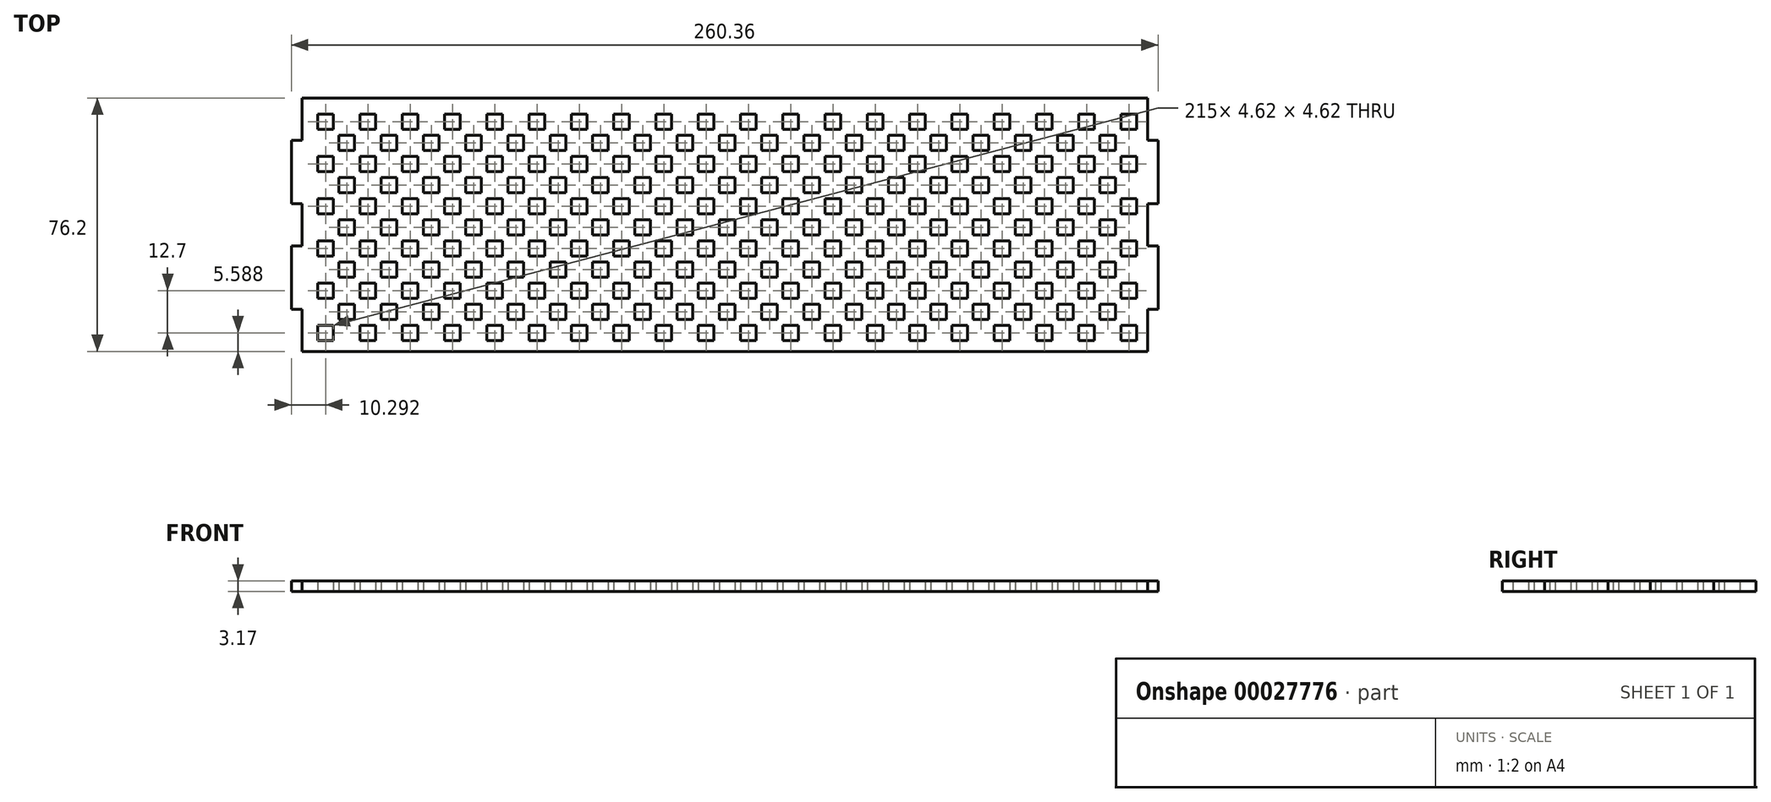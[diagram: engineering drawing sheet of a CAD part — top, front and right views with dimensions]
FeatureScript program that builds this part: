
annotation { "Feature Type Name" : "Feature", "Feature Type Description" : "" }
export const myFeature = defineFeature(function(context is Context, id is Id, definition is map)
    precondition{}
    {
        {
            var Q0;
            Q0=qCreatedBy(makeId("Top.planeOp"),FACE);
            var sketch = newSketch(context, id + "F0", { "sketchPlane" : qUnion([Q0])});
            skLineSegment(sketch, "E0.rect.bottom", {"start": v(-127, 38.1) * mm, "end": v(127, 38.1) * mm});
            skLineSegment(sketch, "E0.rect.top", {"start": v(-127, -38.1) * mm, "end": v(127, -38.1) * mm});
            skLineSegment(sketch, "E0.rect.left", {"start": v(-127, 38.1) * mm, "end": v(-127, 25.4) * mm});
            skLineSegment(sketch, "E0.rect.right", {"start": v(127, 38.1) * mm, "end": v(127, 25.4) * mm});
            skPoint(sketch, "E0.rect.middle", {"position": v(0, 0) * mm});
            skPoint(sketch, "E1", {"position": v(-127, 25.4) * mm});
            skPoint(sketch, "E2", {"position": v(-127, 6.35) * mm});
            skPoint(sketch, "E3", {"position": v(-127, -25.4) * mm});
            skPoint(sketch, "E4", {"position": v(-127, -6.35) * mm});
            skLineSegment(sketch, "E5.bottom", {"start": v(-127, 25.4) * mm, "end": v(-130.18, 25.4) * mm});
            skLineSegment(sketch, "E5.top", {"start": v(-127, 6.35) * mm, "end": v(-130.18, 6.35) * mm});
            skLineSegment(sketch, "E5.right", {"start": v(-130.18, 25.4) * mm, "end": v(-130.18, 6.35) * mm});
            skLineSegment(sketch, "E6.bottom", {"start": v(-127, -6.35) * mm, "end": v(-130.18, -6.35) * mm});
            skLineSegment(sketch, "E6.top", {"start": v(-127, -25.4) * mm, "end": v(-130.18, -25.4) * mm});
            skLineSegment(sketch, "E6.left", {"start": v(-127, -25.4) * mm, "end": v(-127, -25.4) * mm});
            skLineSegment(sketch, "E6.right", {"start": v(-130.18, -6.35) * mm, "end": v(-130.18, -25.4) * mm});
            skLineSegment(sketch, "E7.trimOffspring", {"start": v(-127, 6.35) * mm, "end": v(-127, -6.35) * mm});
            skLineSegment(sketch, "E8.trimOffspring", {"start": v(-127, -25.4) * mm, "end": v(-127, -38.1) * mm});
            skLineSegment(sketch, "E9.MirrorCS", {"start": v(130.18, 25.4) * mm, "end": v(130.18, 6.35) * mm});
            skLineSegment(sketch, "E10.MirrorCS", {"start": v(127, 25.4) * mm, "end": v(130.18, 25.4) * mm});
            skLineSegment(sketch, "E11.MirrorCS", {"start": v(127, 6.35) * mm, "end": v(130.18, 6.35) * mm});
            skLineSegment(sketch, "E12.MirrorCS", {"start": v(127, -6.35) * mm, "end": v(130.18, -6.35) * mm});
            skLineSegment(sketch, "E13.MirrorCS", {"start": v(130.18, -6.35) * mm, "end": v(130.18, -25.4) * mm});
            skLineSegment(sketch, "E14.MirrorCS", {"start": v(127, -25.4) * mm, "end": v(130.18, -25.4) * mm});
            skLineSegment(sketch, "E15.trimOffspring", {"start": v(127, 6.35) * mm, "end": v(127, -6.35) * mm});
            skLineSegment(sketch, "E16.trimOffspring", {"start": v(127, -25.4) * mm, "end": v(127, -38.1) * mm});
            skPoint(sketch, "E17", {"position": v(-127, 33.3) * mm});
            skPoint(sketch, "E18", {"position": v(-122.2, 38.1) * mm});
            skLineSegment(sketch, "E19.bottom", {"start": v(-122.2, 33.3) * mm, "end": v(-117.58, 33.3) * mm});
            skLineSegment(sketch, "E19.top", {"start": v(-122.2, 28.68) * mm, "end": v(-117.58, 28.68) * mm});
            skLineSegment(sketch, "E19.left", {"start": v(-122.2, 33.3) * mm, "end": v(-122.2, 28.68) * mm});
            skLineSegment(sketch, "E19.right", {"start": v(-117.58, 33.3) * mm, "end": v(-117.58, 28.68) * mm});
            skLineSegment(sketch, "E20.0.1.0", {"start": v(-117.58, 20.6) * mm, "end": v(-117.58, 15.98) * mm});
            skLineSegment(sketch, "E20.0.1.1", {"start": v(-122.2, 20.6) * mm, "end": v(-117.58, 20.6) * mm});
            skLineSegment(sketch, "E20.0.1.2", {"start": v(-122.2, 20.6) * mm, "end": v(-122.2, 15.98) * mm});
            skLineSegment(sketch, "E20.0.1.3", {"start": v(-122.2, 15.98) * mm, "end": v(-117.58, 15.98) * mm});
            skLineSegment(sketch, "E20.0.2.0", {"start": v(-117.58, 7.9) * mm, "end": v(-117.58, 3.28) * mm});
            skLineSegment(sketch, "E20.0.2.1", {"start": v(-122.2, 7.9) * mm, "end": v(-117.58, 7.9) * mm});
            skLineSegment(sketch, "E20.0.2.2", {"start": v(-122.2, 7.9) * mm, "end": v(-122.2, 3.28) * mm});
            skLineSegment(sketch, "E20.0.2.3", {"start": v(-122.2, 3.28) * mm, "end": v(-117.58, 3.28) * mm});
            skLineSegment(sketch, "E20.0.3.0", {"start": v(-117.58, -4.8) * mm, "end": v(-117.58, -9.42) * mm});
            skLineSegment(sketch, "E20.0.3.1", {"start": v(-122.2, -4.8) * mm, "end": v(-117.58, -4.8) * mm});
            skLineSegment(sketch, "E20.0.3.2", {"start": v(-122.2, -4.8) * mm, "end": v(-122.2, -9.42) * mm});
            skLineSegment(sketch, "E20.0.3.3", {"start": v(-122.2, -9.42) * mm, "end": v(-117.58, -9.42) * mm});
            skLineSegment(sketch, "E20.0.4.0", {"start": v(-117.58, -17.5) * mm, "end": v(-117.58, -22.12) * mm});
            skLineSegment(sketch, "E20.0.4.1", {"start": v(-122.2, -17.5) * mm, "end": v(-117.58, -17.5) * mm});
            skLineSegment(sketch, "E20.0.4.2", {"start": v(-122.2, -17.5) * mm, "end": v(-122.2, -22.12) * mm});
            skLineSegment(sketch, "E20.0.4.3", {"start": v(-122.2, -22.12) * mm, "end": v(-117.58, -22.12) * mm});
            skLineSegment(sketch, "E20.0.5.0", {"start": v(-117.58, -30.2) * mm, "end": v(-117.58, -34.82) * mm});
            skLineSegment(sketch, "E20.0.5.1", {"start": v(-122.2, -30.2) * mm, "end": v(-117.58, -30.2) * mm});
            skLineSegment(sketch, "E20.0.5.2", {"start": v(-122.2, -30.2) * mm, "end": v(-122.2, -34.82) * mm});
            skLineSegment(sketch, "E20.0.5.3", {"start": v(-122.2, -34.82) * mm, "end": v(-117.58, -34.82) * mm});
            skLineSegment(sketch, "E20.1.0.0", {"start": v(-104.88, 33.3) * mm, "end": v(-104.88, 28.68) * mm});
            skLineSegment(sketch, "E20.1.0.1", {"start": v(-109.5, 33.3) * mm, "end": v(-104.88, 33.3) * mm});
            skLineSegment(sketch, "E20.1.0.2", {"start": v(-109.5, 33.3) * mm, "end": v(-109.5, 28.68) * mm});
            skLineSegment(sketch, "E20.1.0.3", {"start": v(-109.5, 28.68) * mm, "end": v(-104.88, 28.68) * mm});
            skLineSegment(sketch, "E20.1.1.0", {"start": v(-104.88, 20.6) * mm, "end": v(-104.88, 15.98) * mm});
            skLineSegment(sketch, "E20.1.1.1", {"start": v(-109.5, 20.6) * mm, "end": v(-104.88, 20.6) * mm});
            skLineSegment(sketch, "E20.1.1.2", {"start": v(-109.5, 20.6) * mm, "end": v(-109.5, 15.98) * mm});
            skLineSegment(sketch, "E20.1.1.3", {"start": v(-109.5, 15.98) * mm, "end": v(-104.88, 15.98) * mm});
            skLineSegment(sketch, "E20.1.2.0", {"start": v(-104.88, 7.9) * mm, "end": v(-104.88, 3.28) * mm});
            skLineSegment(sketch, "E20.1.2.1", {"start": v(-109.5, 7.9) * mm, "end": v(-104.88, 7.9) * mm});
            skLineSegment(sketch, "E20.1.2.2", {"start": v(-109.5, 7.9) * mm, "end": v(-109.5, 3.28) * mm});
            skLineSegment(sketch, "E20.1.2.3", {"start": v(-109.5, 3.28) * mm, "end": v(-104.88, 3.28) * mm});
            skLineSegment(sketch, "E20.1.3.0", {"start": v(-104.88, -4.8) * mm, "end": v(-104.88, -9.42) * mm});
            skLineSegment(sketch, "E20.1.3.1", {"start": v(-109.5, -4.8) * mm, "end": v(-104.88, -4.8) * mm});
            skLineSegment(sketch, "E20.1.3.2", {"start": v(-109.5, -4.8) * mm, "end": v(-109.5, -9.42) * mm});
            skLineSegment(sketch, "E20.1.3.3", {"start": v(-109.5, -9.42) * mm, "end": v(-104.88, -9.42) * mm});
            skLineSegment(sketch, "E20.1.4.0", {"start": v(-104.88, -17.5) * mm, "end": v(-104.88, -22.12) * mm});
            skLineSegment(sketch, "E20.1.4.1", {"start": v(-109.5, -17.5) * mm, "end": v(-104.88, -17.5) * mm});
            skLineSegment(sketch, "E20.1.4.2", {"start": v(-109.5, -17.5) * mm, "end": v(-109.5, -22.12) * mm});
            skLineSegment(sketch, "E20.1.4.3", {"start": v(-109.5, -22.12) * mm, "end": v(-104.88, -22.12) * mm});
            skLineSegment(sketch, "E20.1.5.0", {"start": v(-104.88, -30.2) * mm, "end": v(-104.88, -34.82) * mm});
            skLineSegment(sketch, "E20.1.5.1", {"start": v(-109.5, -30.2) * mm, "end": v(-104.88, -30.2) * mm});
            skLineSegment(sketch, "E20.1.5.2", {"start": v(-109.5, -30.2) * mm, "end": v(-109.5, -34.82) * mm});
            skLineSegment(sketch, "E20.1.5.3", {"start": v(-109.5, -34.82) * mm, "end": v(-104.88, -34.82) * mm});
            skLineSegment(sketch, "E20.2.0.0", {"start": v(-92.18, 33.3) * mm, "end": v(-92.18, 28.68) * mm});
            skLineSegment(sketch, "E20.2.0.1", {"start": v(-96.8, 33.3) * mm, "end": v(-92.18, 33.3) * mm});
            skLineSegment(sketch, "E20.2.0.2", {"start": v(-96.8, 33.3) * mm, "end": v(-96.8, 28.68) * mm});
            skLineSegment(sketch, "E20.2.0.3", {"start": v(-96.8, 28.68) * mm, "end": v(-92.18, 28.68) * mm});
            skLineSegment(sketch, "E20.2.1.0", {"start": v(-92.18, 20.6) * mm, "end": v(-92.18, 15.98) * mm});
            skLineSegment(sketch, "E20.2.1.1", {"start": v(-96.8, 20.6) * mm, "end": v(-92.18, 20.6) * mm});
            skLineSegment(sketch, "E20.2.1.2", {"start": v(-96.8, 20.6) * mm, "end": v(-96.8, 15.98) * mm});
            skLineSegment(sketch, "E20.2.1.3", {"start": v(-96.8, 15.98) * mm, "end": v(-92.18, 15.98) * mm});
            skLineSegment(sketch, "E20.2.2.0", {"start": v(-92.18, 7.9) * mm, "end": v(-92.18, 3.28) * mm});
            skLineSegment(sketch, "E20.2.2.1", {"start": v(-96.8, 7.9) * mm, "end": v(-92.18, 7.9) * mm});
            skLineSegment(sketch, "E20.2.2.2", {"start": v(-96.8, 7.9) * mm, "end": v(-96.8, 3.28) * mm});
            skLineSegment(sketch, "E20.2.2.3", {"start": v(-96.8, 3.28) * mm, "end": v(-92.18, 3.28) * mm});
            skLineSegment(sketch, "E20.2.3.0", {"start": v(-92.18, -4.8) * mm, "end": v(-92.18, -9.42) * mm});
            skLineSegment(sketch, "E20.2.3.1", {"start": v(-96.8, -4.8) * mm, "end": v(-92.18, -4.8) * mm});
            skLineSegment(sketch, "E20.2.3.2", {"start": v(-96.8, -4.8) * mm, "end": v(-96.8, -9.42) * mm});
            skLineSegment(sketch, "E20.2.3.3", {"start": v(-96.8, -9.42) * mm, "end": v(-92.18, -9.42) * mm});
            skLineSegment(sketch, "E20.2.4.0", {"start": v(-92.18, -17.5) * mm, "end": v(-92.18, -22.12) * mm});
            skLineSegment(sketch, "E20.2.4.1", {"start": v(-96.8, -17.5) * mm, "end": v(-92.18, -17.5) * mm});
            skLineSegment(sketch, "E20.2.4.2", {"start": v(-96.8, -17.5) * mm, "end": v(-96.8, -22.12) * mm});
            skLineSegment(sketch, "E20.2.4.3", {"start": v(-96.8, -22.12) * mm, "end": v(-92.18, -22.12) * mm});
            skLineSegment(sketch, "E20.2.5.0", {"start": v(-92.18, -30.2) * mm, "end": v(-92.18, -34.82) * mm});
            skLineSegment(sketch, "E20.2.5.1", {"start": v(-96.8, -30.2) * mm, "end": v(-92.18, -30.2) * mm});
            skLineSegment(sketch, "E20.2.5.2", {"start": v(-96.8, -30.2) * mm, "end": v(-96.8, -34.82) * mm});
            skLineSegment(sketch, "E20.2.5.3", {"start": v(-96.8, -34.82) * mm, "end": v(-92.18, -34.82) * mm});
            skLineSegment(sketch, "E20.3.0.0", {"start": v(-79.48, 33.3) * mm, "end": v(-79.48, 28.68) * mm});
            skLineSegment(sketch, "E20.3.0.1", {"start": v(-84.1, 33.3) * mm, "end": v(-79.48, 33.3) * mm});
            skLineSegment(sketch, "E20.3.0.2", {"start": v(-84.1, 33.3) * mm, "end": v(-84.1, 28.68) * mm});
            skLineSegment(sketch, "E20.3.0.3", {"start": v(-84.1, 28.68) * mm, "end": v(-79.48, 28.68) * mm});
            skLineSegment(sketch, "E20.3.1.0", {"start": v(-79.48, 20.6) * mm, "end": v(-79.48, 15.98) * mm});
            skLineSegment(sketch, "E20.3.1.1", {"start": v(-84.1, 20.6) * mm, "end": v(-79.48, 20.6) * mm});
            skLineSegment(sketch, "E20.3.1.2", {"start": v(-84.1, 20.6) * mm, "end": v(-84.1, 15.98) * mm});
            skLineSegment(sketch, "E20.3.1.3", {"start": v(-84.1, 15.98) * mm, "end": v(-79.48, 15.98) * mm});
            skLineSegment(sketch, "E20.3.2.0", {"start": v(-79.48, 7.9) * mm, "end": v(-79.48, 3.28) * mm});
            skLineSegment(sketch, "E20.3.2.1", {"start": v(-84.1, 7.9) * mm, "end": v(-79.48, 7.9) * mm});
            skLineSegment(sketch, "E20.3.2.2", {"start": v(-84.1, 7.9) * mm, "end": v(-84.1, 3.28) * mm});
            skLineSegment(sketch, "E20.3.2.3", {"start": v(-84.1, 3.28) * mm, "end": v(-79.48, 3.28) * mm});
            skLineSegment(sketch, "E20.3.3.0", {"start": v(-79.48, -4.8) * mm, "end": v(-79.48, -9.42) * mm});
            skLineSegment(sketch, "E20.3.3.1", {"start": v(-84.1, -4.8) * mm, "end": v(-79.48, -4.8) * mm});
            skLineSegment(sketch, "E20.3.3.2", {"start": v(-84.1, -4.8) * mm, "end": v(-84.1, -9.42) * mm});
            skLineSegment(sketch, "E20.3.3.3", {"start": v(-84.1, -9.42) * mm, "end": v(-79.48, -9.42) * mm});
            skLineSegment(sketch, "E20.3.4.0", {"start": v(-79.48, -17.5) * mm, "end": v(-79.48, -22.12) * mm});
            skLineSegment(sketch, "E20.3.4.1", {"start": v(-84.1, -17.5) * mm, "end": v(-79.48, -17.5) * mm});
            skLineSegment(sketch, "E20.3.4.2", {"start": v(-84.1, -17.5) * mm, "end": v(-84.1, -22.12) * mm});
            skLineSegment(sketch, "E20.3.4.3", {"start": v(-84.1, -22.12) * mm, "end": v(-79.48, -22.12) * mm});
            skLineSegment(sketch, "E20.3.5.0", {"start": v(-79.48, -30.2) * mm, "end": v(-79.48, -34.82) * mm});
            skLineSegment(sketch, "E20.3.5.1", {"start": v(-84.1, -30.2) * mm, "end": v(-79.48, -30.2) * mm});
            skLineSegment(sketch, "E20.3.5.2", {"start": v(-84.1, -30.2) * mm, "end": v(-84.1, -34.82) * mm});
            skLineSegment(sketch, "E20.3.5.3", {"start": v(-84.1, -34.82) * mm, "end": v(-79.48, -34.82) * mm});
            skLineSegment(sketch, "E20.4.0.0", {"start": v(-66.78, 33.3) * mm, "end": v(-66.78, 28.68) * mm});
            skLineSegment(sketch, "E20.4.0.1", {"start": v(-71.4, 33.3) * mm, "end": v(-66.78, 33.3) * mm});
            skLineSegment(sketch, "E20.4.0.2", {"start": v(-71.4, 33.3) * mm, "end": v(-71.4, 28.68) * mm});
            skLineSegment(sketch, "E20.4.0.3", {"start": v(-71.4, 28.68) * mm, "end": v(-66.78, 28.68) * mm});
            skLineSegment(sketch, "E20.4.1.0", {"start": v(-66.78, 20.6) * mm, "end": v(-66.78, 15.98) * mm});
            skLineSegment(sketch, "E20.4.1.1", {"start": v(-71.4, 20.6) * mm, "end": v(-66.78, 20.6) * mm});
            skLineSegment(sketch, "E20.4.1.2", {"start": v(-71.4, 20.6) * mm, "end": v(-71.4, 15.98) * mm});
            skLineSegment(sketch, "E20.4.1.3", {"start": v(-71.4, 15.98) * mm, "end": v(-66.78, 15.98) * mm});
            skLineSegment(sketch, "E20.4.2.0", {"start": v(-66.78, 7.9) * mm, "end": v(-66.78, 3.28) * mm});
            skLineSegment(sketch, "E20.4.2.1", {"start": v(-71.4, 7.9) * mm, "end": v(-66.78, 7.9) * mm});
            skLineSegment(sketch, "E20.4.2.2", {"start": v(-71.4, 7.9) * mm, "end": v(-71.4, 3.28) * mm});
            skLineSegment(sketch, "E20.4.2.3", {"start": v(-71.4, 3.28) * mm, "end": v(-66.78, 3.28) * mm});
            skLineSegment(sketch, "E20.4.3.0", {"start": v(-66.78, -4.8) * mm, "end": v(-66.78, -9.42) * mm});
            skLineSegment(sketch, "E20.4.3.1", {"start": v(-71.4, -4.8) * mm, "end": v(-66.78, -4.8) * mm});
            skLineSegment(sketch, "E20.4.3.2", {"start": v(-71.4, -4.8) * mm, "end": v(-71.4, -9.42) * mm});
            skLineSegment(sketch, "E20.4.3.3", {"start": v(-71.4, -9.42) * mm, "end": v(-66.78, -9.42) * mm});
            skLineSegment(sketch, "E20.4.4.0", {"start": v(-66.78, -17.5) * mm, "end": v(-66.78, -22.12) * mm});
            skLineSegment(sketch, "E20.4.4.1", {"start": v(-71.4, -17.5) * mm, "end": v(-66.78, -17.5) * mm});
            skLineSegment(sketch, "E20.4.4.2", {"start": v(-71.4, -17.5) * mm, "end": v(-71.4, -22.12) * mm});
            skLineSegment(sketch, "E20.4.4.3", {"start": v(-71.4, -22.12) * mm, "end": v(-66.78, -22.12) * mm});
            skLineSegment(sketch, "E20.4.5.0", {"start": v(-66.78, -30.2) * mm, "end": v(-66.78, -34.82) * mm});
            skLineSegment(sketch, "E20.4.5.1", {"start": v(-71.4, -30.2) * mm, "end": v(-66.78, -30.2) * mm});
            skLineSegment(sketch, "E20.4.5.2", {"start": v(-71.4, -30.2) * mm, "end": v(-71.4, -34.82) * mm});
            skLineSegment(sketch, "E20.4.5.3", {"start": v(-71.4, -34.82) * mm, "end": v(-66.78, -34.82) * mm});
            skLineSegment(sketch, "E20.5.0.0", {"start": v(-54.08, 33.3) * mm, "end": v(-54.08, 28.68) * mm});
            skLineSegment(sketch, "E20.5.0.1", {"start": v(-58.7, 33.3) * mm, "end": v(-54.08, 33.3) * mm});
            skLineSegment(sketch, "E20.5.0.2", {"start": v(-58.7, 33.3) * mm, "end": v(-58.7, 28.68) * mm});
            skLineSegment(sketch, "E20.5.0.3", {"start": v(-58.7, 28.68) * mm, "end": v(-54.08, 28.68) * mm});
            skLineSegment(sketch, "E20.5.1.0", {"start": v(-54.08, 20.6) * mm, "end": v(-54.08, 15.98) * mm});
            skLineSegment(sketch, "E20.5.1.1", {"start": v(-58.7, 20.6) * mm, "end": v(-54.08, 20.6) * mm});
            skLineSegment(sketch, "E20.5.1.2", {"start": v(-58.7, 20.6) * mm, "end": v(-58.7, 15.98) * mm});
            skLineSegment(sketch, "E20.5.1.3", {"start": v(-58.7, 15.98) * mm, "end": v(-54.08, 15.98) * mm});
            skLineSegment(sketch, "E20.5.2.0", {"start": v(-54.08, 7.9) * mm, "end": v(-54.08, 3.28) * mm});
            skLineSegment(sketch, "E20.5.2.1", {"start": v(-58.7, 7.9) * mm, "end": v(-54.08, 7.9) * mm});
            skLineSegment(sketch, "E20.5.2.2", {"start": v(-58.7, 7.9) * mm, "end": v(-58.7, 3.28) * mm});
            skLineSegment(sketch, "E20.5.2.3", {"start": v(-58.7, 3.28) * mm, "end": v(-54.08, 3.28) * mm});
            skLineSegment(sketch, "E20.5.3.0", {"start": v(-54.08, -4.8) * mm, "end": v(-54.08, -9.42) * mm});
            skLineSegment(sketch, "E20.5.3.1", {"start": v(-58.7, -4.8) * mm, "end": v(-54.08, -4.8) * mm});
            skLineSegment(sketch, "E20.5.3.2", {"start": v(-58.7, -4.8) * mm, "end": v(-58.7, -9.42) * mm});
            skLineSegment(sketch, "E20.5.3.3", {"start": v(-58.7, -9.42) * mm, "end": v(-54.08, -9.42) * mm});
            skLineSegment(sketch, "E20.5.4.0", {"start": v(-54.08, -17.5) * mm, "end": v(-54.08, -22.12) * mm});
            skLineSegment(sketch, "E20.5.4.1", {"start": v(-58.7, -17.5) * mm, "end": v(-54.08, -17.5) * mm});
            skLineSegment(sketch, "E20.5.4.2", {"start": v(-58.7, -17.5) * mm, "end": v(-58.7, -22.12) * mm});
            skLineSegment(sketch, "E20.5.4.3", {"start": v(-58.7, -22.12) * mm, "end": v(-54.08, -22.12) * mm});
            skLineSegment(sketch, "E20.5.5.0", {"start": v(-54.08, -30.2) * mm, "end": v(-54.08, -34.82) * mm});
            skLineSegment(sketch, "E20.5.5.1", {"start": v(-58.7, -30.2) * mm, "end": v(-54.08, -30.2) * mm});
            skLineSegment(sketch, "E20.5.5.2", {"start": v(-58.7, -30.2) * mm, "end": v(-58.7, -34.82) * mm});
            skLineSegment(sketch, "E20.5.5.3", {"start": v(-58.7, -34.82) * mm, "end": v(-54.08, -34.82) * mm});
            skLineSegment(sketch, "E20.6.0.0", {"start": v(-41.38, 33.3) * mm, "end": v(-41.38, 28.68) * mm});
            skLineSegment(sketch, "E20.6.0.1", {"start": v(-46, 33.3) * mm, "end": v(-41.38, 33.3) * mm});
            skLineSegment(sketch, "E20.6.0.2", {"start": v(-46, 33.3) * mm, "end": v(-46, 28.68) * mm});
            skLineSegment(sketch, "E20.6.0.3", {"start": v(-46, 28.68) * mm, "end": v(-41.38, 28.68) * mm});
            skLineSegment(sketch, "E20.6.1.0", {"start": v(-41.38, 20.6) * mm, "end": v(-41.38, 15.98) * mm});
            skLineSegment(sketch, "E20.6.1.1", {"start": v(-46, 20.6) * mm, "end": v(-41.38, 20.6) * mm});
            skLineSegment(sketch, "E20.6.1.2", {"start": v(-46, 20.6) * mm, "end": v(-46, 15.98) * mm});
            skLineSegment(sketch, "E20.6.1.3", {"start": v(-46, 15.98) * mm, "end": v(-41.38, 15.98) * mm});
            skLineSegment(sketch, "E20.6.2.0", {"start": v(-41.38, 7.9) * mm, "end": v(-41.38, 3.28) * mm});
            skLineSegment(sketch, "E20.6.2.1", {"start": v(-46, 7.9) * mm, "end": v(-41.38, 7.9) * mm});
            skLineSegment(sketch, "E20.6.2.2", {"start": v(-46, 7.9) * mm, "end": v(-46, 3.28) * mm});
            skLineSegment(sketch, "E20.6.2.3", {"start": v(-46, 3.28) * mm, "end": v(-41.38, 3.28) * mm});
            skLineSegment(sketch, "E20.6.3.0", {"start": v(-41.38, -4.8) * mm, "end": v(-41.38, -9.42) * mm});
            skLineSegment(sketch, "E20.6.3.1", {"start": v(-46, -4.8) * mm, "end": v(-41.38, -4.8) * mm});
            skLineSegment(sketch, "E20.6.3.2", {"start": v(-46, -4.8) * mm, "end": v(-46, -9.42) * mm});
            skLineSegment(sketch, "E20.6.3.3", {"start": v(-46, -9.42) * mm, "end": v(-41.38, -9.42) * mm});
            skLineSegment(sketch, "E20.6.4.0", {"start": v(-41.38, -17.5) * mm, "end": v(-41.38, -22.12) * mm});
            skLineSegment(sketch, "E20.6.4.1", {"start": v(-46, -17.5) * mm, "end": v(-41.38, -17.5) * mm});
            skLineSegment(sketch, "E20.6.4.2", {"start": v(-46, -17.5) * mm, "end": v(-46, -22.12) * mm});
            skLineSegment(sketch, "E20.6.4.3", {"start": v(-46, -22.12) * mm, "end": v(-41.38, -22.12) * mm});
            skLineSegment(sketch, "E20.6.5.0", {"start": v(-41.38, -30.2) * mm, "end": v(-41.38, -34.82) * mm});
            skLineSegment(sketch, "E20.6.5.1", {"start": v(-46, -30.2) * mm, "end": v(-41.38, -30.2) * mm});
            skLineSegment(sketch, "E20.6.5.2", {"start": v(-46, -30.2) * mm, "end": v(-46, -34.82) * mm});
            skLineSegment(sketch, "E20.6.5.3", {"start": v(-46, -34.82) * mm, "end": v(-41.38, -34.82) * mm});
            skLineSegment(sketch, "E20.7.0.0", {"start": v(-28.68, 33.3) * mm, "end": v(-28.68, 28.68) * mm});
            skLineSegment(sketch, "E20.7.0.1", {"start": v(-33.3, 33.3) * mm, "end": v(-28.68, 33.3) * mm});
            skLineSegment(sketch, "E20.7.0.2", {"start": v(-33.3, 33.3) * mm, "end": v(-33.3, 28.68) * mm});
            skLineSegment(sketch, "E20.7.0.3", {"start": v(-33.3, 28.68) * mm, "end": v(-28.68, 28.68) * mm});
            skLineSegment(sketch, "E20.7.1.0", {"start": v(-28.68, 20.6) * mm, "end": v(-28.68, 15.98) * mm});
            skLineSegment(sketch, "E20.7.1.1", {"start": v(-33.3, 20.6) * mm, "end": v(-28.68, 20.6) * mm});
            skLineSegment(sketch, "E20.7.1.2", {"start": v(-33.3, 20.6) * mm, "end": v(-33.3, 15.98) * mm});
            skLineSegment(sketch, "E20.7.1.3", {"start": v(-33.3, 15.98) * mm, "end": v(-28.68, 15.98) * mm});
            skLineSegment(sketch, "E20.7.2.0", {"start": v(-28.68, 7.9) * mm, "end": v(-28.68, 3.28) * mm});
            skLineSegment(sketch, "E20.7.2.1", {"start": v(-33.3, 7.9) * mm, "end": v(-28.68, 7.9) * mm});
            skLineSegment(sketch, "E20.7.2.2", {"start": v(-33.3, 7.9) * mm, "end": v(-33.3, 3.28) * mm});
            skLineSegment(sketch, "E20.7.2.3", {"start": v(-33.3, 3.28) * mm, "end": v(-28.68, 3.28) * mm});
            skLineSegment(sketch, "E20.7.3.0", {"start": v(-28.68, -4.8) * mm, "end": v(-28.68, -9.42) * mm});
            skLineSegment(sketch, "E20.7.3.1", {"start": v(-33.3, -4.8) * mm, "end": v(-28.68, -4.8) * mm});
            skLineSegment(sketch, "E20.7.3.2", {"start": v(-33.3, -4.8) * mm, "end": v(-33.3, -9.42) * mm});
            skLineSegment(sketch, "E20.7.3.3", {"start": v(-33.3, -9.42) * mm, "end": v(-28.68, -9.42) * mm});
            skLineSegment(sketch, "E20.7.4.0", {"start": v(-28.68, -17.5) * mm, "end": v(-28.68, -22.12) * mm});
            skLineSegment(sketch, "E20.7.4.1", {"start": v(-33.3, -17.5) * mm, "end": v(-28.68, -17.5) * mm});
            skLineSegment(sketch, "E20.7.4.2", {"start": v(-33.3, -17.5) * mm, "end": v(-33.3, -22.12) * mm});
            skLineSegment(sketch, "E20.7.4.3", {"start": v(-33.3, -22.12) * mm, "end": v(-28.68, -22.12) * mm});
            skLineSegment(sketch, "E20.7.5.0", {"start": v(-28.68, -30.2) * mm, "end": v(-28.68, -34.82) * mm});
            skLineSegment(sketch, "E20.7.5.1", {"start": v(-33.3, -30.2) * mm, "end": v(-28.68, -30.2) * mm});
            skLineSegment(sketch, "E20.7.5.2", {"start": v(-33.3, -30.2) * mm, "end": v(-33.3, -34.82) * mm});
            skLineSegment(sketch, "E20.7.5.3", {"start": v(-33.3, -34.82) * mm, "end": v(-28.68, -34.82) * mm});
            skLineSegment(sketch, "E20.8.0.0", {"start": v(-15.98, 33.3) * mm, "end": v(-15.98, 28.68) * mm});
            skLineSegment(sketch, "E20.8.0.1", {"start": v(-20.6, 33.3) * mm, "end": v(-15.98, 33.3) * mm});
            skLineSegment(sketch, "E20.8.0.2", {"start": v(-20.6, 33.3) * mm, "end": v(-20.6, 28.68) * mm});
            skLineSegment(sketch, "E20.8.0.3", {"start": v(-20.6, 28.68) * mm, "end": v(-15.98, 28.68) * mm});
            skLineSegment(sketch, "E20.8.1.0", {"start": v(-15.98, 20.6) * mm, "end": v(-15.98, 15.98) * mm});
            skLineSegment(sketch, "E20.8.1.1", {"start": v(-20.6, 20.6) * mm, "end": v(-15.98, 20.6) * mm});
            skLineSegment(sketch, "E20.8.1.2", {"start": v(-20.6, 20.6) * mm, "end": v(-20.6, 15.98) * mm});
            skLineSegment(sketch, "E20.8.1.3", {"start": v(-20.6, 15.98) * mm, "end": v(-15.98, 15.98) * mm});
            skLineSegment(sketch, "E20.8.2.0", {"start": v(-15.98, 7.9) * mm, "end": v(-15.98, 3.28) * mm});
            skLineSegment(sketch, "E20.8.2.1", {"start": v(-20.6, 7.9) * mm, "end": v(-15.98, 7.9) * mm});
            skLineSegment(sketch, "E20.8.2.2", {"start": v(-20.6, 7.9) * mm, "end": v(-20.6, 3.28) * mm});
            skLineSegment(sketch, "E20.8.2.3", {"start": v(-20.6, 3.28) * mm, "end": v(-15.98, 3.28) * mm});
            skLineSegment(sketch, "E20.8.3.0", {"start": v(-15.98, -4.8) * mm, "end": v(-15.98, -9.42) * mm});
            skLineSegment(sketch, "E20.8.3.1", {"start": v(-20.6, -4.8) * mm, "end": v(-15.98, -4.8) * mm});
            skLineSegment(sketch, "E20.8.3.2", {"start": v(-20.6, -4.8) * mm, "end": v(-20.6, -9.42) * mm});
            skLineSegment(sketch, "E20.8.3.3", {"start": v(-20.6, -9.42) * mm, "end": v(-15.98, -9.42) * mm});
            skLineSegment(sketch, "E20.8.4.0", {"start": v(-15.98, -17.5) * mm, "end": v(-15.98, -22.12) * mm});
            skLineSegment(sketch, "E20.8.4.1", {"start": v(-20.6, -17.5) * mm, "end": v(-15.98, -17.5) * mm});
            skLineSegment(sketch, "E20.8.4.2", {"start": v(-20.6, -17.5) * mm, "end": v(-20.6, -22.12) * mm});
            skLineSegment(sketch, "E20.8.4.3", {"start": v(-20.6, -22.12) * mm, "end": v(-15.98, -22.12) * mm});
            skLineSegment(sketch, "E20.8.5.0", {"start": v(-15.98, -30.2) * mm, "end": v(-15.98, -34.82) * mm});
            skLineSegment(sketch, "E20.8.5.1", {"start": v(-20.6, -30.2) * mm, "end": v(-15.98, -30.2) * mm});
            skLineSegment(sketch, "E20.8.5.2", {"start": v(-20.6, -30.2) * mm, "end": v(-20.6, -34.82) * mm});
            skLineSegment(sketch, "E20.8.5.3", {"start": v(-20.6, -34.82) * mm, "end": v(-15.98, -34.82) * mm});
            skLineSegment(sketch, "E20.9.0.0", {"start": v(-3.28, 33.3) * mm, "end": v(-3.28, 28.68) * mm});
            skLineSegment(sketch, "E20.9.0.1", {"start": v(-7.9, 33.3) * mm, "end": v(-3.28, 33.3) * mm});
            skLineSegment(sketch, "E20.9.0.2", {"start": v(-7.9, 33.3) * mm, "end": v(-7.9, 28.68) * mm});
            skLineSegment(sketch, "E20.9.0.3", {"start": v(-7.9, 28.68) * mm, "end": v(-3.28, 28.68) * mm});
            skLineSegment(sketch, "E20.9.1.0", {"start": v(-3.28, 20.6) * mm, "end": v(-3.28, 15.98) * mm});
            skLineSegment(sketch, "E20.9.1.1", {"start": v(-7.9, 20.6) * mm, "end": v(-3.28, 20.6) * mm});
            skLineSegment(sketch, "E20.9.1.2", {"start": v(-7.9, 20.6) * mm, "end": v(-7.9, 15.98) * mm});
            skLineSegment(sketch, "E20.9.1.3", {"start": v(-7.9, 15.98) * mm, "end": v(-3.28, 15.98) * mm});
            skLineSegment(sketch, "E20.9.2.0", {"start": v(-3.28, 7.9) * mm, "end": v(-3.28, 3.28) * mm});
            skLineSegment(sketch, "E20.9.2.1", {"start": v(-7.9, 7.9) * mm, "end": v(-3.28, 7.9) * mm});
            skLineSegment(sketch, "E20.9.2.2", {"start": v(-7.9, 7.9) * mm, "end": v(-7.9, 3.28) * mm});
            skLineSegment(sketch, "E20.9.2.3", {"start": v(-7.9, 3.28) * mm, "end": v(-3.28, 3.28) * mm});
            skLineSegment(sketch, "E20.9.3.0", {"start": v(-3.28, -4.8) * mm, "end": v(-3.28, -9.42) * mm});
            skLineSegment(sketch, "E20.9.3.1", {"start": v(-7.9, -4.8) * mm, "end": v(-3.28, -4.8) * mm});
            skLineSegment(sketch, "E20.9.3.2", {"start": v(-7.9, -4.8) * mm, "end": v(-7.9, -9.42) * mm});
            skLineSegment(sketch, "E20.9.3.3", {"start": v(-7.9, -9.42) * mm, "end": v(-3.28, -9.42) * mm});
            skLineSegment(sketch, "E20.9.4.0", {"start": v(-3.28, -17.5) * mm, "end": v(-3.28, -22.12) * mm});
            skLineSegment(sketch, "E20.9.4.1", {"start": v(-7.9, -17.5) * mm, "end": v(-3.28, -17.5) * mm});
            skLineSegment(sketch, "E20.9.4.2", {"start": v(-7.9, -17.5) * mm, "end": v(-7.9, -22.12) * mm});
            skLineSegment(sketch, "E20.9.4.3", {"start": v(-7.9, -22.12) * mm, "end": v(-3.28, -22.12) * mm});
            skLineSegment(sketch, "E20.9.5.0", {"start": v(-3.28, -30.2) * mm, "end": v(-3.28, -34.82) * mm});
            skLineSegment(sketch, "E20.9.5.1", {"start": v(-7.9, -30.2) * mm, "end": v(-3.28, -30.2) * mm});
            skLineSegment(sketch, "E20.9.5.2", {"start": v(-7.9, -30.2) * mm, "end": v(-7.9, -34.82) * mm});
            skLineSegment(sketch, "E20.9.5.3", {"start": v(-7.9, -34.82) * mm, "end": v(-3.28, -34.82) * mm});
            skLineSegment(sketch, "E20.10.0.0", {"start": v(9.42, 33.3) * mm, "end": v(9.42, 28.68) * mm});
            skLineSegment(sketch, "E20.10.0.1", {"start": v(4.8, 33.3) * mm, "end": v(9.42, 33.3) * mm});
            skLineSegment(sketch, "E20.10.0.2", {"start": v(4.8, 33.3) * mm, "end": v(4.8, 28.68) * mm});
            skLineSegment(sketch, "E20.10.0.3", {"start": v(4.8, 28.68) * mm, "end": v(9.42, 28.68) * mm});
            skLineSegment(sketch, "E20.10.1.0", {"start": v(9.42, 20.6) * mm, "end": v(9.42, 15.98) * mm});
            skLineSegment(sketch, "E20.10.1.1", {"start": v(4.8, 20.6) * mm, "end": v(9.42, 20.6) * mm});
            skLineSegment(sketch, "E20.10.1.2", {"start": v(4.8, 20.6) * mm, "end": v(4.8, 15.98) * mm});
            skLineSegment(sketch, "E20.10.1.3", {"start": v(4.8, 15.98) * mm, "end": v(9.42, 15.98) * mm});
            skLineSegment(sketch, "E20.10.2.0", {"start": v(9.42, 7.9) * mm, "end": v(9.42, 3.28) * mm});
            skLineSegment(sketch, "E20.10.2.1", {"start": v(4.8, 7.9) * mm, "end": v(9.42, 7.9) * mm});
            skLineSegment(sketch, "E20.10.2.2", {"start": v(4.8, 7.9) * mm, "end": v(4.8, 3.28) * mm});
            skLineSegment(sketch, "E20.10.2.3", {"start": v(4.8, 3.28) * mm, "end": v(9.42, 3.28) * mm});
            skLineSegment(sketch, "E20.10.3.0", {"start": v(9.42, -4.8) * mm, "end": v(9.42, -9.42) * mm});
            skLineSegment(sketch, "E20.10.3.1", {"start": v(4.8, -4.8) * mm, "end": v(9.42, -4.8) * mm});
            skLineSegment(sketch, "E20.10.3.2", {"start": v(4.8, -4.8) * mm, "end": v(4.8, -9.42) * mm});
            skLineSegment(sketch, "E20.10.3.3", {"start": v(4.8, -9.42) * mm, "end": v(9.42, -9.42) * mm});
            skLineSegment(sketch, "E20.10.4.0", {"start": v(9.42, -17.5) * mm, "end": v(9.42, -22.12) * mm});
            skLineSegment(sketch, "E20.10.4.1", {"start": v(4.8, -17.5) * mm, "end": v(9.42, -17.5) * mm});
            skLineSegment(sketch, "E20.10.4.2", {"start": v(4.8, -17.5) * mm, "end": v(4.8, -22.12) * mm});
            skLineSegment(sketch, "E20.10.4.3", {"start": v(4.8, -22.12) * mm, "end": v(9.42, -22.12) * mm});
            skLineSegment(sketch, "E20.10.5.0", {"start": v(9.42, -30.2) * mm, "end": v(9.42, -34.82) * mm});
            skLineSegment(sketch, "E20.10.5.1", {"start": v(4.8, -30.2) * mm, "end": v(9.42, -30.2) * mm});
            skLineSegment(sketch, "E20.10.5.2", {"start": v(4.8, -30.2) * mm, "end": v(4.8, -34.82) * mm});
            skLineSegment(sketch, "E20.10.5.3", {"start": v(4.8, -34.82) * mm, "end": v(9.42, -34.82) * mm});
            skLineSegment(sketch, "E20.11.0.0", {"start": v(22.12, 33.3) * mm, "end": v(22.12, 28.68) * mm});
            skLineSegment(sketch, "E20.11.0.1", {"start": v(17.5, 33.3) * mm, "end": v(22.12, 33.3) * mm});
            skLineSegment(sketch, "E20.11.0.2", {"start": v(17.5, 33.3) * mm, "end": v(17.5, 28.68) * mm});
            skLineSegment(sketch, "E20.11.0.3", {"start": v(17.5, 28.68) * mm, "end": v(22.12, 28.68) * mm});
            skLineSegment(sketch, "E20.11.1.0", {"start": v(22.12, 20.6) * mm, "end": v(22.12, 15.98) * mm});
            skLineSegment(sketch, "E20.11.1.1", {"start": v(17.5, 20.6) * mm, "end": v(22.12, 20.6) * mm});
            skLineSegment(sketch, "E20.11.1.2", {"start": v(17.5, 20.6) * mm, "end": v(17.5, 15.98) * mm});
            skLineSegment(sketch, "E20.11.1.3", {"start": v(17.5, 15.98) * mm, "end": v(22.12, 15.98) * mm});
            skLineSegment(sketch, "E20.11.2.0", {"start": v(22.12, 7.9) * mm, "end": v(22.12, 3.28) * mm});
            skLineSegment(sketch, "E20.11.2.1", {"start": v(17.5, 7.9) * mm, "end": v(22.12, 7.9) * mm});
            skLineSegment(sketch, "E20.11.2.2", {"start": v(17.5, 7.9) * mm, "end": v(17.5, 3.28) * mm});
            skLineSegment(sketch, "E20.11.2.3", {"start": v(17.5, 3.28) * mm, "end": v(22.12, 3.28) * mm});
            skLineSegment(sketch, "E20.11.3.0", {"start": v(22.12, -4.8) * mm, "end": v(22.12, -9.42) * mm});
            skLineSegment(sketch, "E20.11.3.1", {"start": v(17.5, -4.8) * mm, "end": v(22.12, -4.8) * mm});
            skLineSegment(sketch, "E20.11.3.2", {"start": v(17.5, -4.8) * mm, "end": v(17.5, -9.42) * mm});
            skLineSegment(sketch, "E20.11.3.3", {"start": v(17.5, -9.42) * mm, "end": v(22.12, -9.42) * mm});
            skLineSegment(sketch, "E20.11.4.0", {"start": v(22.12, -17.5) * mm, "end": v(22.12, -22.12) * mm});
            skLineSegment(sketch, "E20.11.4.1", {"start": v(17.5, -17.5) * mm, "end": v(22.12, -17.5) * mm});
            skLineSegment(sketch, "E20.11.4.2", {"start": v(17.5, -17.5) * mm, "end": v(17.5, -22.12) * mm});
            skLineSegment(sketch, "E20.11.4.3", {"start": v(17.5, -22.12) * mm, "end": v(22.12, -22.12) * mm});
            skLineSegment(sketch, "E20.11.5.0", {"start": v(22.12, -30.2) * mm, "end": v(22.12, -34.82) * mm});
            skLineSegment(sketch, "E20.11.5.1", {"start": v(17.5, -30.2) * mm, "end": v(22.12, -30.2) * mm});
            skLineSegment(sketch, "E20.11.5.2", {"start": v(17.5, -30.2) * mm, "end": v(17.5, -34.82) * mm});
            skLineSegment(sketch, "E20.11.5.3", {"start": v(17.5, -34.82) * mm, "end": v(22.12, -34.82) * mm});
            skLineSegment(sketch, "E20.12.0.0", {"start": v(34.82, 33.3) * mm, "end": v(34.82, 28.68) * mm});
            skLineSegment(sketch, "E20.12.0.1", {"start": v(30.2, 33.3) * mm, "end": v(34.82, 33.3) * mm});
            skLineSegment(sketch, "E20.12.0.2", {"start": v(30.2, 33.3) * mm, "end": v(30.2, 28.68) * mm});
            skLineSegment(sketch, "E20.12.0.3", {"start": v(30.2, 28.68) * mm, "end": v(34.82, 28.68) * mm});
            skLineSegment(sketch, "E20.12.1.0", {"start": v(34.82, 20.6) * mm, "end": v(34.82, 15.98) * mm});
            skLineSegment(sketch, "E20.12.1.1", {"start": v(30.2, 20.6) * mm, "end": v(34.82, 20.6) * mm});
            skLineSegment(sketch, "E20.12.1.2", {"start": v(30.2, 20.6) * mm, "end": v(30.2, 15.98) * mm});
            skLineSegment(sketch, "E20.12.1.3", {"start": v(30.2, 15.98) * mm, "end": v(34.82, 15.98) * mm});
            skLineSegment(sketch, "E20.12.2.0", {"start": v(34.82, 7.9) * mm, "end": v(34.82, 3.28) * mm});
            skLineSegment(sketch, "E20.12.2.1", {"start": v(30.2, 7.9) * mm, "end": v(34.82, 7.9) * mm});
            skLineSegment(sketch, "E20.12.2.2", {"start": v(30.2, 7.9) * mm, "end": v(30.2, 3.28) * mm});
            skLineSegment(sketch, "E20.12.2.3", {"start": v(30.2, 3.28) * mm, "end": v(34.82, 3.28) * mm});
            skLineSegment(sketch, "E20.12.3.0", {"start": v(34.82, -4.8) * mm, "end": v(34.82, -9.42) * mm});
            skLineSegment(sketch, "E20.12.3.1", {"start": v(30.2, -4.8) * mm, "end": v(34.82, -4.8) * mm});
            skLineSegment(sketch, "E20.12.3.2", {"start": v(30.2, -4.8) * mm, "end": v(30.2, -9.42) * mm});
            skLineSegment(sketch, "E20.12.3.3", {"start": v(30.2, -9.42) * mm, "end": v(34.82, -9.42) * mm});
            skLineSegment(sketch, "E20.12.4.0", {"start": v(34.82, -17.5) * mm, "end": v(34.82, -22.12) * mm});
            skLineSegment(sketch, "E20.12.4.1", {"start": v(30.2, -17.5) * mm, "end": v(34.82, -17.5) * mm});
            skLineSegment(sketch, "E20.12.4.2", {"start": v(30.2, -17.5) * mm, "end": v(30.2, -22.12) * mm});
            skLineSegment(sketch, "E20.12.4.3", {"start": v(30.2, -22.12) * mm, "end": v(34.82, -22.12) * mm});
            skLineSegment(sketch, "E20.12.5.0", {"start": v(34.82, -30.2) * mm, "end": v(34.82, -34.82) * mm});
            skLineSegment(sketch, "E20.12.5.1", {"start": v(30.2, -30.2) * mm, "end": v(34.82, -30.2) * mm});
            skLineSegment(sketch, "E20.12.5.2", {"start": v(30.2, -30.2) * mm, "end": v(30.2, -34.82) * mm});
            skLineSegment(sketch, "E20.12.5.3", {"start": v(30.2, -34.82) * mm, "end": v(34.82, -34.82) * mm});
            skLineSegment(sketch, "E20.13.0.0", {"start": v(47.52, 33.3) * mm, "end": v(47.52, 28.68) * mm});
            skLineSegment(sketch, "E20.13.0.1", {"start": v(42.9, 33.3) * mm, "end": v(47.52, 33.3) * mm});
            skLineSegment(sketch, "E20.13.0.2", {"start": v(42.9, 33.3) * mm, "end": v(42.9, 28.68) * mm});
            skLineSegment(sketch, "E20.13.0.3", {"start": v(42.9, 28.68) * mm, "end": v(47.52, 28.68) * mm});
            skLineSegment(sketch, "E20.13.1.0", {"start": v(47.52, 20.6) * mm, "end": v(47.52, 15.98) * mm});
            skLineSegment(sketch, "E20.13.1.1", {"start": v(42.9, 20.6) * mm, "end": v(47.52, 20.6) * mm});
            skLineSegment(sketch, "E20.13.1.2", {"start": v(42.9, 20.6) * mm, "end": v(42.9, 15.98) * mm});
            skLineSegment(sketch, "E20.13.1.3", {"start": v(42.9, 15.98) * mm, "end": v(47.52, 15.98) * mm});
            skLineSegment(sketch, "E20.13.2.0", {"start": v(47.52, 7.9) * mm, "end": v(47.52, 3.28) * mm});
            skLineSegment(sketch, "E20.13.2.1", {"start": v(42.9, 7.9) * mm, "end": v(47.52, 7.9) * mm});
            skLineSegment(sketch, "E20.13.2.2", {"start": v(42.9, 7.9) * mm, "end": v(42.9, 3.28) * mm});
            skLineSegment(sketch, "E20.13.2.3", {"start": v(42.9, 3.28) * mm, "end": v(47.52, 3.28) * mm});
            skLineSegment(sketch, "E20.13.3.0", {"start": v(47.52, -4.8) * mm, "end": v(47.52, -9.42) * mm});
            skLineSegment(sketch, "E20.13.3.1", {"start": v(42.9, -4.8) * mm, "end": v(47.52, -4.8) * mm});
            skLineSegment(sketch, "E20.13.3.2", {"start": v(42.9, -4.8) * mm, "end": v(42.9, -9.42) * mm});
            skLineSegment(sketch, "E20.13.3.3", {"start": v(42.9, -9.42) * mm, "end": v(47.52, -9.42) * mm});
            skLineSegment(sketch, "E20.13.4.0", {"start": v(47.52, -17.5) * mm, "end": v(47.52, -22.12) * mm});
            skLineSegment(sketch, "E20.13.4.1", {"start": v(42.9, -17.5) * mm, "end": v(47.52, -17.5) * mm});
            skLineSegment(sketch, "E20.13.4.2", {"start": v(42.9, -17.5) * mm, "end": v(42.9, -22.12) * mm});
            skLineSegment(sketch, "E20.13.4.3", {"start": v(42.9, -22.12) * mm, "end": v(47.52, -22.12) * mm});
            skLineSegment(sketch, "E20.13.5.0", {"start": v(47.52, -30.2) * mm, "end": v(47.52, -34.82) * mm});
            skLineSegment(sketch, "E20.13.5.1", {"start": v(42.9, -30.2) * mm, "end": v(47.52, -30.2) * mm});
            skLineSegment(sketch, "E20.13.5.2", {"start": v(42.9, -30.2) * mm, "end": v(42.9, -34.82) * mm});
            skLineSegment(sketch, "E20.13.5.3", {"start": v(42.9, -34.82) * mm, "end": v(47.52, -34.82) * mm});
            skLineSegment(sketch, "E20.14.0.0", {"start": v(60.22, 33.3) * mm, "end": v(60.22, 28.68) * mm});
            skLineSegment(sketch, "E20.14.0.1", {"start": v(55.6, 33.3) * mm, "end": v(60.22, 33.3) * mm});
            skLineSegment(sketch, "E20.14.0.2", {"start": v(55.6, 33.3) * mm, "end": v(55.6, 28.68) * mm});
            skLineSegment(sketch, "E20.14.0.3", {"start": v(55.6, 28.68) * mm, "end": v(60.22, 28.68) * mm});
            skLineSegment(sketch, "E20.14.1.0", {"start": v(60.22, 20.6) * mm, "end": v(60.22, 15.98) * mm});
            skLineSegment(sketch, "E20.14.1.1", {"start": v(55.6, 20.6) * mm, "end": v(60.22, 20.6) * mm});
            skLineSegment(sketch, "E20.14.1.2", {"start": v(55.6, 20.6) * mm, "end": v(55.6, 15.98) * mm});
            skLineSegment(sketch, "E20.14.1.3", {"start": v(55.6, 15.98) * mm, "end": v(60.22, 15.98) * mm});
            skLineSegment(sketch, "E20.14.2.0", {"start": v(60.22, 7.9) * mm, "end": v(60.22, 3.28) * mm});
            skLineSegment(sketch, "E20.14.2.1", {"start": v(55.6, 7.9) * mm, "end": v(60.22, 7.9) * mm});
            skLineSegment(sketch, "E20.14.2.2", {"start": v(55.6, 7.9) * mm, "end": v(55.6, 3.28) * mm});
            skLineSegment(sketch, "E20.14.2.3", {"start": v(55.6, 3.28) * mm, "end": v(60.22, 3.28) * mm});
            skLineSegment(sketch, "E20.14.3.0", {"start": v(60.22, -4.8) * mm, "end": v(60.22, -9.42) * mm});
            skLineSegment(sketch, "E20.14.3.1", {"start": v(55.6, -4.8) * mm, "end": v(60.22, -4.8) * mm});
            skLineSegment(sketch, "E20.14.3.2", {"start": v(55.6, -4.8) * mm, "end": v(55.6, -9.42) * mm});
            skLineSegment(sketch, "E20.14.3.3", {"start": v(55.6, -9.42) * mm, "end": v(60.22, -9.42) * mm});
            skLineSegment(sketch, "E20.14.4.0", {"start": v(60.22, -17.5) * mm, "end": v(60.22, -22.12) * mm});
            skLineSegment(sketch, "E20.14.4.1", {"start": v(55.6, -17.5) * mm, "end": v(60.22, -17.5) * mm});
            skLineSegment(sketch, "E20.14.4.2", {"start": v(55.6, -17.5) * mm, "end": v(55.6, -22.12) * mm});
            skLineSegment(sketch, "E20.14.4.3", {"start": v(55.6, -22.12) * mm, "end": v(60.22, -22.12) * mm});
            skLineSegment(sketch, "E20.14.5.0", {"start": v(60.22, -30.2) * mm, "end": v(60.22, -34.82) * mm});
            skLineSegment(sketch, "E20.14.5.1", {"start": v(55.6, -30.2) * mm, "end": v(60.22, -30.2) * mm});
            skLineSegment(sketch, "E20.14.5.2", {"start": v(55.6, -30.2) * mm, "end": v(55.6, -34.82) * mm});
            skLineSegment(sketch, "E20.14.5.3", {"start": v(55.6, -34.82) * mm, "end": v(60.22, -34.82) * mm});
            skLineSegment(sketch, "E20.15.0.0", {"start": v(72.92, 33.3) * mm, "end": v(72.92, 28.68) * mm});
            skLineSegment(sketch, "E20.15.0.1", {"start": v(68.3, 33.3) * mm, "end": v(72.92, 33.3) * mm});
            skLineSegment(sketch, "E20.15.0.2", {"start": v(68.3, 33.3) * mm, "end": v(68.3, 28.68) * mm});
            skLineSegment(sketch, "E20.15.0.3", {"start": v(68.3, 28.68) * mm, "end": v(72.92, 28.68) * mm});
            skLineSegment(sketch, "E20.15.1.0", {"start": v(72.92, 20.6) * mm, "end": v(72.92, 15.98) * mm});
            skLineSegment(sketch, "E20.15.1.1", {"start": v(68.3, 20.6) * mm, "end": v(72.92, 20.6) * mm});
            skLineSegment(sketch, "E20.15.1.2", {"start": v(68.3, 20.6) * mm, "end": v(68.3, 15.98) * mm});
            skLineSegment(sketch, "E20.15.1.3", {"start": v(68.3, 15.98) * mm, "end": v(72.92, 15.98) * mm});
            skLineSegment(sketch, "E20.15.2.0", {"start": v(72.92, 7.9) * mm, "end": v(72.92, 3.28) * mm});
            skLineSegment(sketch, "E20.15.2.1", {"start": v(68.3, 7.9) * mm, "end": v(72.92, 7.9) * mm});
            skLineSegment(sketch, "E20.15.2.2", {"start": v(68.3, 7.9) * mm, "end": v(68.3, 3.28) * mm});
            skLineSegment(sketch, "E20.15.2.3", {"start": v(68.3, 3.28) * mm, "end": v(72.92, 3.28) * mm});
            skLineSegment(sketch, "E20.15.3.0", {"start": v(72.92, -4.8) * mm, "end": v(72.92, -9.42) * mm});
            skLineSegment(sketch, "E20.15.3.1", {"start": v(68.3, -4.8) * mm, "end": v(72.92, -4.8) * mm});
            skLineSegment(sketch, "E20.15.3.2", {"start": v(68.3, -4.8) * mm, "end": v(68.3, -9.42) * mm});
            skLineSegment(sketch, "E20.15.3.3", {"start": v(68.3, -9.42) * mm, "end": v(72.92, -9.42) * mm});
            skLineSegment(sketch, "E20.15.4.0", {"start": v(72.92, -17.5) * mm, "end": v(72.92, -22.12) * mm});
            skLineSegment(sketch, "E20.15.4.1", {"start": v(68.3, -17.5) * mm, "end": v(72.92, -17.5) * mm});
            skLineSegment(sketch, "E20.15.4.2", {"start": v(68.3, -17.5) * mm, "end": v(68.3, -22.12) * mm});
            skLineSegment(sketch, "E20.15.4.3", {"start": v(68.3, -22.12) * mm, "end": v(72.92, -22.12) * mm});
            skLineSegment(sketch, "E20.15.5.0", {"start": v(72.92, -30.2) * mm, "end": v(72.92, -34.82) * mm});
            skLineSegment(sketch, "E20.15.5.1", {"start": v(68.3, -30.2) * mm, "end": v(72.92, -30.2) * mm});
            skLineSegment(sketch, "E20.15.5.2", {"start": v(68.3, -30.2) * mm, "end": v(68.3, -34.82) * mm});
            skLineSegment(sketch, "E20.15.5.3", {"start": v(68.3, -34.82) * mm, "end": v(72.92, -34.82) * mm});
            skLineSegment(sketch, "E20.16.0.0", {"start": v(85.62, 33.3) * mm, "end": v(85.62, 28.68) * mm});
            skLineSegment(sketch, "E20.16.0.1", {"start": v(81, 33.3) * mm, "end": v(85.62, 33.3) * mm});
            skLineSegment(sketch, "E20.16.0.2", {"start": v(81, 33.3) * mm, "end": v(81, 28.68) * mm});
            skLineSegment(sketch, "E20.16.0.3", {"start": v(81, 28.68) * mm, "end": v(85.62, 28.68) * mm});
            skLineSegment(sketch, "E20.16.1.0", {"start": v(85.62, 20.6) * mm, "end": v(85.62, 15.98) * mm});
            skLineSegment(sketch, "E20.16.1.1", {"start": v(81, 20.6) * mm, "end": v(85.62, 20.6) * mm});
            skLineSegment(sketch, "E20.16.1.2", {"start": v(81, 20.6) * mm, "end": v(81, 15.98) * mm});
            skLineSegment(sketch, "E20.16.1.3", {"start": v(81, 15.98) * mm, "end": v(85.62, 15.98) * mm});
            skLineSegment(sketch, "E20.16.2.0", {"start": v(85.62, 7.9) * mm, "end": v(85.62, 3.28) * mm});
            skLineSegment(sketch, "E20.16.2.1", {"start": v(81, 7.9) * mm, "end": v(85.62, 7.9) * mm});
            skLineSegment(sketch, "E20.16.2.2", {"start": v(81, 7.9) * mm, "end": v(81, 3.28) * mm});
            skLineSegment(sketch, "E20.16.2.3", {"start": v(81, 3.28) * mm, "end": v(85.62, 3.28) * mm});
            skLineSegment(sketch, "E20.16.3.0", {"start": v(85.62, -4.8) * mm, "end": v(85.62, -9.42) * mm});
            skLineSegment(sketch, "E20.16.3.1", {"start": v(81, -4.8) * mm, "end": v(85.62, -4.8) * mm});
            skLineSegment(sketch, "E20.16.3.2", {"start": v(81, -4.8) * mm, "end": v(81, -9.42) * mm});
            skLineSegment(sketch, "E20.16.3.3", {"start": v(81, -9.42) * mm, "end": v(85.62, -9.42) * mm});
            skLineSegment(sketch, "E20.16.4.0", {"start": v(85.62, -17.5) * mm, "end": v(85.62, -22.12) * mm});
            skLineSegment(sketch, "E20.16.4.1", {"start": v(81, -17.5) * mm, "end": v(85.62, -17.5) * mm});
            skLineSegment(sketch, "E20.16.4.2", {"start": v(81, -17.5) * mm, "end": v(81, -22.12) * mm});
            skLineSegment(sketch, "E20.16.4.3", {"start": v(81, -22.12) * mm, "end": v(85.62, -22.12) * mm});
            skLineSegment(sketch, "E20.16.5.0", {"start": v(85.62, -30.2) * mm, "end": v(85.62, -34.82) * mm});
            skLineSegment(sketch, "E20.16.5.1", {"start": v(81, -30.2) * mm, "end": v(85.62, -30.2) * mm});
            skLineSegment(sketch, "E20.16.5.2", {"start": v(81, -30.2) * mm, "end": v(81, -34.82) * mm});
            skLineSegment(sketch, "E20.16.5.3", {"start": v(81, -34.82) * mm, "end": v(85.62, -34.82) * mm});
            skLineSegment(sketch, "E20.17.0.0", {"start": v(98.32, 33.3) * mm, "end": v(98.32, 28.68) * mm});
            skLineSegment(sketch, "E20.17.0.1", {"start": v(93.7, 33.3) * mm, "end": v(98.32, 33.3) * mm});
            skLineSegment(sketch, "E20.17.0.2", {"start": v(93.7, 33.3) * mm, "end": v(93.7, 28.68) * mm});
            skLineSegment(sketch, "E20.17.0.3", {"start": v(93.7, 28.68) * mm, "end": v(98.32, 28.68) * mm});
            skLineSegment(sketch, "E20.17.1.0", {"start": v(98.32, 20.6) * mm, "end": v(98.32, 15.98) * mm});
            skLineSegment(sketch, "E20.17.1.1", {"start": v(93.7, 20.6) * mm, "end": v(98.32, 20.6) * mm});
            skLineSegment(sketch, "E20.17.1.2", {"start": v(93.7, 20.6) * mm, "end": v(93.7, 15.98) * mm});
            skLineSegment(sketch, "E20.17.1.3", {"start": v(93.7, 15.98) * mm, "end": v(98.32, 15.98) * mm});
            skLineSegment(sketch, "E20.17.2.0", {"start": v(98.32, 7.9) * mm, "end": v(98.32, 3.28) * mm});
            skLineSegment(sketch, "E20.17.2.1", {"start": v(93.7, 7.9) * mm, "end": v(98.32, 7.9) * mm});
            skLineSegment(sketch, "E20.17.2.2", {"start": v(93.7, 7.9) * mm, "end": v(93.7, 3.28) * mm});
            skLineSegment(sketch, "E20.17.2.3", {"start": v(93.7, 3.28) * mm, "end": v(98.32, 3.28) * mm});
            skLineSegment(sketch, "E20.17.3.0", {"start": v(98.32, -4.8) * mm, "end": v(98.32, -9.42) * mm});
            skLineSegment(sketch, "E20.17.3.1", {"start": v(93.7, -4.8) * mm, "end": v(98.32, -4.8) * mm});
            skLineSegment(sketch, "E20.17.3.2", {"start": v(93.7, -4.8) * mm, "end": v(93.7, -9.42) * mm});
            skLineSegment(sketch, "E20.17.3.3", {"start": v(93.7, -9.42) * mm, "end": v(98.32, -9.42) * mm});
            skLineSegment(sketch, "E20.17.4.0", {"start": v(98.32, -17.5) * mm, "end": v(98.32, -22.12) * mm});
            skLineSegment(sketch, "E20.17.4.1", {"start": v(93.7, -17.5) * mm, "end": v(98.32, -17.5) * mm});
            skLineSegment(sketch, "E20.17.4.2", {"start": v(93.7, -17.5) * mm, "end": v(93.7, -22.12) * mm});
            skLineSegment(sketch, "E20.17.4.3", {"start": v(93.7, -22.12) * mm, "end": v(98.32, -22.12) * mm});
            skLineSegment(sketch, "E20.17.5.0", {"start": v(98.32, -30.2) * mm, "end": v(98.32, -34.82) * mm});
            skLineSegment(sketch, "E20.17.5.1", {"start": v(93.7, -30.2) * mm, "end": v(98.32, -30.2) * mm});
            skLineSegment(sketch, "E20.17.5.2", {"start": v(93.7, -30.2) * mm, "end": v(93.7, -34.82) * mm});
            skLineSegment(sketch, "E20.17.5.3", {"start": v(93.7, -34.82) * mm, "end": v(98.32, -34.82) * mm});
            skLineSegment(sketch, "E20.18.0.0", {"start": v(111.02, 33.3) * mm, "end": v(111.02, 28.68) * mm});
            skLineSegment(sketch, "E20.18.0.1", {"start": v(106.4, 33.3) * mm, "end": v(111.02, 33.3) * mm});
            skLineSegment(sketch, "E20.18.0.2", {"start": v(106.4, 33.3) * mm, "end": v(106.4, 28.68) * mm});
            skLineSegment(sketch, "E20.18.0.3", {"start": v(106.4, 28.68) * mm, "end": v(111.02, 28.68) * mm});
            skLineSegment(sketch, "E20.18.1.0", {"start": v(111.02, 20.6) * mm, "end": v(111.02, 15.98) * mm});
            skLineSegment(sketch, "E20.18.1.1", {"start": v(106.4, 20.6) * mm, "end": v(111.02, 20.6) * mm});
            skLineSegment(sketch, "E20.18.1.2", {"start": v(106.4, 20.6) * mm, "end": v(106.4, 15.98) * mm});
            skLineSegment(sketch, "E20.18.1.3", {"start": v(106.4, 15.98) * mm, "end": v(111.02, 15.98) * mm});
            skLineSegment(sketch, "E20.18.2.0", {"start": v(111.02, 7.9) * mm, "end": v(111.02, 3.28) * mm});
            skLineSegment(sketch, "E20.18.2.1", {"start": v(106.4, 7.9) * mm, "end": v(111.02, 7.9) * mm});
            skLineSegment(sketch, "E20.18.2.2", {"start": v(106.4, 7.9) * mm, "end": v(106.4, 3.28) * mm});
            skLineSegment(sketch, "E20.18.2.3", {"start": v(106.4, 3.28) * mm, "end": v(111.02, 3.28) * mm});
            skLineSegment(sketch, "E20.18.3.0", {"start": v(111.02, -4.8) * mm, "end": v(111.02, -9.42) * mm});
            skLineSegment(sketch, "E20.18.3.1", {"start": v(106.4, -4.8) * mm, "end": v(111.02, -4.8) * mm});
            skLineSegment(sketch, "E20.18.3.2", {"start": v(106.4, -4.8) * mm, "end": v(106.4, -9.42) * mm});
            skLineSegment(sketch, "E20.18.3.3", {"start": v(106.4, -9.42) * mm, "end": v(111.02, -9.42) * mm});
            skLineSegment(sketch, "E20.18.4.0", {"start": v(111.02, -17.5) * mm, "end": v(111.02, -22.12) * mm});
            skLineSegment(sketch, "E20.18.4.1", {"start": v(106.4, -17.5) * mm, "end": v(111.02, -17.5) * mm});
            skLineSegment(sketch, "E20.18.4.2", {"start": v(106.4, -17.5) * mm, "end": v(106.4, -22.12) * mm});
            skLineSegment(sketch, "E20.18.4.3", {"start": v(106.4, -22.12) * mm, "end": v(111.02, -22.12) * mm});
            skLineSegment(sketch, "E20.18.5.0", {"start": v(111.02, -30.2) * mm, "end": v(111.02, -34.82) * mm});
            skLineSegment(sketch, "E20.18.5.1", {"start": v(106.4, -30.2) * mm, "end": v(111.02, -30.2) * mm});
            skLineSegment(sketch, "E20.18.5.2", {"start": v(106.4, -30.2) * mm, "end": v(106.4, -34.82) * mm});
            skLineSegment(sketch, "E20.18.5.3", {"start": v(106.4, -34.82) * mm, "end": v(111.02, -34.82) * mm});
            skLineSegment(sketch, "E20.19.0.0", {"start": v(123.72, 33.3) * mm, "end": v(123.72, 28.68) * mm});
            skLineSegment(sketch, "E20.19.0.1", {"start": v(119.1, 33.3) * mm, "end": v(123.72, 33.3) * mm});
            skLineSegment(sketch, "E20.19.0.2", {"start": v(119.1, 33.3) * mm, "end": v(119.1, 28.68) * mm});
            skLineSegment(sketch, "E20.19.0.3", {"start": v(119.1, 28.68) * mm, "end": v(123.72, 28.68) * mm});
            skLineSegment(sketch, "E20.19.1.0", {"start": v(123.72, 20.6) * mm, "end": v(123.72, 15.98) * mm});
            skLineSegment(sketch, "E20.19.1.1", {"start": v(119.1, 20.6) * mm, "end": v(123.72, 20.6) * mm});
            skLineSegment(sketch, "E20.19.1.2", {"start": v(119.1, 20.6) * mm, "end": v(119.1, 15.98) * mm});
            skLineSegment(sketch, "E20.19.1.3", {"start": v(119.1, 15.98) * mm, "end": v(123.72, 15.98) * mm});
            skLineSegment(sketch, "E20.19.2.0", {"start": v(123.72, 7.9) * mm, "end": v(123.72, 3.28) * mm});
            skLineSegment(sketch, "E20.19.2.1", {"start": v(119.1, 7.9) * mm, "end": v(123.72, 7.9) * mm});
            skLineSegment(sketch, "E20.19.2.2", {"start": v(119.1, 7.9) * mm, "end": v(119.1, 3.28) * mm});
            skLineSegment(sketch, "E20.19.2.3", {"start": v(119.1, 3.28) * mm, "end": v(123.72, 3.28) * mm});
            skLineSegment(sketch, "E20.19.3.0", {"start": v(123.72, -4.8) * mm, "end": v(123.72, -9.42) * mm});
            skLineSegment(sketch, "E20.19.3.1", {"start": v(119.1, -4.8) * mm, "end": v(123.72, -4.8) * mm});
            skLineSegment(sketch, "E20.19.3.2", {"start": v(119.1, -4.8) * mm, "end": v(119.1, -9.42) * mm});
            skLineSegment(sketch, "E20.19.3.3", {"start": v(119.1, -9.42) * mm, "end": v(123.72, -9.42) * mm});
            skLineSegment(sketch, "E20.19.4.0", {"start": v(123.72, -17.5) * mm, "end": v(123.72, -22.12) * mm});
            skLineSegment(sketch, "E20.19.4.1", {"start": v(119.1, -17.5) * mm, "end": v(123.72, -17.5) * mm});
            skLineSegment(sketch, "E20.19.4.2", {"start": v(119.1, -17.5) * mm, "end": v(119.1, -22.12) * mm});
            skLineSegment(sketch, "E20.19.4.3", {"start": v(119.1, -22.12) * mm, "end": v(123.72, -22.12) * mm});
            skLineSegment(sketch, "E20.19.5.0", {"start": v(123.72, -30.2) * mm, "end": v(123.72, -34.82) * mm});
            skLineSegment(sketch, "E20.19.5.1", {"start": v(119.1, -30.2) * mm, "end": v(123.72, -30.2) * mm});
            skLineSegment(sketch, "E20.19.5.2", {"start": v(119.1, -30.2) * mm, "end": v(119.1, -34.82) * mm});
            skLineSegment(sketch, "E20.19.5.3", {"start": v(119.1, -34.82) * mm, "end": v(123.72, -34.82) * mm});
            skLineSegment(sketch, "E20.direction1", {"start": v(-117.58, 28.68) * mm, "end": v(-104.88, 28.68) * mm, "construction": true});
            skLineSegment(sketch, "E20.direction2", {"start": v(-117.58, 28.68) * mm, "end": v(-117.58, 15.98) * mm, "construction": true});
            skLineSegment(sketch, "E21.top", {"start": v(-117.58, 20.6) * mm, "end": v(-109.5, 20.6) * mm});
            skLineSegment(sketch, "E21.left", {"start": v(-117.58, 28.68) * mm, "end": v(-117.58, 20.6) * mm});
            skLineSegment(sketch, "E21.right", {"start": v(-109.5, 28.68) * mm, "end": v(-109.5, 20.6) * mm});
            skLineSegment(sketch, "E22.rect.bottom", {"start": v(-111.23, 22.33) * mm, "end": v(-115.85, 22.33) * mm});
            skLineSegment(sketch, "E22.rect.top", {"start": v(-111.23, 26.95) * mm, "end": v(-115.85, 26.95) * mm});
            skLineSegment(sketch, "E22.rect.left", {"start": v(-111.23, 22.33) * mm, "end": v(-111.23, 26.95) * mm});
            skLineSegment(sketch, "E22.rect.right", {"start": v(-115.85, 22.33) * mm, "end": v(-115.85, 26.95) * mm});
            skPoint(sketch, "E22.rect.middle", {"position": v(-113.54, 24.64) * mm});
            skPoint(sketch, "E22.rect.middle.positionSnap0", {"position": v(-117.58, 24.64) * mm});
            skPoint(sketch, "E22.rect.middle.positionSnap1", {"position": v(-113.54, 28.68) * mm});
            skPoint(sketch, "E22.rect.centerSnap0", {"position": v(-117.58, 24.64) * mm});
            skPoint(sketch, "E22.rect.centerSnap1", {"position": v(-113.54, 28.68) * mm});
            skLineSegment(sketch, "E23.0.1.0", {"start": v(-111.23, 14.25) * mm, "end": v(-115.85, 14.25) * mm});
            skLineSegment(sketch, "E23.0.1.1", {"start": v(-111.23, 9.63) * mm, "end": v(-111.23, 14.25) * mm});
            skLineSegment(sketch, "E23.0.1.2", {"start": v(-111.23, 9.63) * mm, "end": v(-115.85, 9.63) * mm});
            skLineSegment(sketch, "E23.0.1.3", {"start": v(-115.85, 9.63) * mm, "end": v(-115.85, 14.25) * mm});
            skLineSegment(sketch, "E23.0.2.0", {"start": v(-111.23, 1.55) * mm, "end": v(-115.85, 1.55) * mm});
            skLineSegment(sketch, "E23.0.2.1", {"start": v(-111.23, -3.07) * mm, "end": v(-111.23, 1.55) * mm});
            skLineSegment(sketch, "E23.0.2.2", {"start": v(-111.23, -3.07) * mm, "end": v(-115.85, -3.07) * mm});
            skLineSegment(sketch, "E23.0.2.3", {"start": v(-115.85, -3.07) * mm, "end": v(-115.85, 1.55) * mm});
            skLineSegment(sketch, "E23.0.3.0", {"start": v(-111.23, -11.15) * mm, "end": v(-115.85, -11.15) * mm});
            skLineSegment(sketch, "E23.0.3.1", {"start": v(-111.23, -15.77) * mm, "end": v(-111.23, -11.15) * mm});
            skLineSegment(sketch, "E23.0.3.2", {"start": v(-111.23, -15.77) * mm, "end": v(-115.85, -15.77) * mm});
            skLineSegment(sketch, "E23.0.3.3", {"start": v(-115.85, -15.77) * mm, "end": v(-115.85, -11.15) * mm});
            skLineSegment(sketch, "E23.0.4.0", {"start": v(-111.23, -23.85) * mm, "end": v(-115.85, -23.85) * mm});
            skLineSegment(sketch, "E23.0.4.1", {"start": v(-111.23, -28.47) * mm, "end": v(-111.23, -23.85) * mm});
            skLineSegment(sketch, "E23.0.4.2", {"start": v(-111.23, -28.47) * mm, "end": v(-115.85, -28.47) * mm});
            skLineSegment(sketch, "E23.0.4.3", {"start": v(-115.85, -28.47) * mm, "end": v(-115.85, -23.85) * mm});
            skLineSegment(sketch, "E23.1.0.0", {"start": v(-98.53, 26.95) * mm, "end": v(-103.15, 26.95) * mm});
            skLineSegment(sketch, "E23.1.0.1", {"start": v(-98.53, 22.33) * mm, "end": v(-98.53, 26.95) * mm});
            skLineSegment(sketch, "E23.1.0.2", {"start": v(-98.53, 22.33) * mm, "end": v(-103.15, 22.33) * mm});
            skLineSegment(sketch, "E23.1.0.3", {"start": v(-103.15, 22.33) * mm, "end": v(-103.15, 26.95) * mm});
            skLineSegment(sketch, "E23.1.1.0", {"start": v(-98.53, 14.25) * mm, "end": v(-103.15, 14.25) * mm});
            skLineSegment(sketch, "E23.1.1.1", {"start": v(-98.53, 9.63) * mm, "end": v(-98.53, 14.25) * mm});
            skLineSegment(sketch, "E23.1.1.2", {"start": v(-98.53, 9.63) * mm, "end": v(-103.15, 9.63) * mm});
            skLineSegment(sketch, "E23.1.1.3", {"start": v(-103.15, 9.63) * mm, "end": v(-103.15, 14.25) * mm});
            skLineSegment(sketch, "E23.1.2.0", {"start": v(-98.53, 1.55) * mm, "end": v(-103.15, 1.55) * mm});
            skLineSegment(sketch, "E23.1.2.1", {"start": v(-98.53, -3.07) * mm, "end": v(-98.53, 1.55) * mm});
            skLineSegment(sketch, "E23.1.2.2", {"start": v(-98.53, -3.07) * mm, "end": v(-103.15, -3.07) * mm});
            skLineSegment(sketch, "E23.1.2.3", {"start": v(-103.15, -3.07) * mm, "end": v(-103.15, 1.55) * mm});
            skLineSegment(sketch, "E23.1.3.0", {"start": v(-98.53, -11.15) * mm, "end": v(-103.15, -11.15) * mm});
            skLineSegment(sketch, "E23.1.3.1", {"start": v(-98.53, -15.77) * mm, "end": v(-98.53, -11.15) * mm});
            skLineSegment(sketch, "E23.1.3.2", {"start": v(-98.53, -15.77) * mm, "end": v(-103.15, -15.77) * mm});
            skLineSegment(sketch, "E23.1.3.3", {"start": v(-103.15, -15.77) * mm, "end": v(-103.15, -11.15) * mm});
            skLineSegment(sketch, "E23.1.4.0", {"start": v(-98.53, -23.85) * mm, "end": v(-103.15, -23.85) * mm});
            skLineSegment(sketch, "E23.1.4.1", {"start": v(-98.53, -28.47) * mm, "end": v(-98.53, -23.85) * mm});
            skLineSegment(sketch, "E23.1.4.2", {"start": v(-98.53, -28.47) * mm, "end": v(-103.15, -28.47) * mm});
            skLineSegment(sketch, "E23.1.4.3", {"start": v(-103.15, -28.47) * mm, "end": v(-103.15, -23.85) * mm});
            skLineSegment(sketch, "E23.2.0.0", {"start": v(-85.83, 26.95) * mm, "end": v(-90.45, 26.95) * mm});
            skLineSegment(sketch, "E23.2.0.1", {"start": v(-85.83, 22.33) * mm, "end": v(-85.83, 26.95) * mm});
            skLineSegment(sketch, "E23.2.0.2", {"start": v(-85.83, 22.33) * mm, "end": v(-90.45, 22.33) * mm});
            skLineSegment(sketch, "E23.2.0.3", {"start": v(-90.45, 22.33) * mm, "end": v(-90.45, 26.95) * mm});
            skLineSegment(sketch, "E23.2.1.0", {"start": v(-85.83, 14.25) * mm, "end": v(-90.45, 14.25) * mm});
            skLineSegment(sketch, "E23.2.1.1", {"start": v(-85.83, 9.63) * mm, "end": v(-85.83, 14.25) * mm});
            skLineSegment(sketch, "E23.2.1.2", {"start": v(-85.83, 9.63) * mm, "end": v(-90.45, 9.63) * mm});
            skLineSegment(sketch, "E23.2.1.3", {"start": v(-90.45, 9.63) * mm, "end": v(-90.45, 14.25) * mm});
            skLineSegment(sketch, "E23.2.2.0", {"start": v(-85.83, 1.55) * mm, "end": v(-90.45, 1.55) * mm});
            skLineSegment(sketch, "E23.2.2.1", {"start": v(-85.83, -3.07) * mm, "end": v(-85.83, 1.55) * mm});
            skLineSegment(sketch, "E23.2.2.2", {"start": v(-85.83, -3.07) * mm, "end": v(-90.45, -3.07) * mm});
            skLineSegment(sketch, "E23.2.2.3", {"start": v(-90.45, -3.07) * mm, "end": v(-90.45, 1.55) * mm});
            skLineSegment(sketch, "E23.2.3.0", {"start": v(-85.83, -11.15) * mm, "end": v(-90.45, -11.15) * mm});
            skLineSegment(sketch, "E23.2.3.1", {"start": v(-85.83, -15.77) * mm, "end": v(-85.83, -11.15) * mm});
            skLineSegment(sketch, "E23.2.3.2", {"start": v(-85.83, -15.77) * mm, "end": v(-90.45, -15.77) * mm});
            skLineSegment(sketch, "E23.2.3.3", {"start": v(-90.45, -15.77) * mm, "end": v(-90.45, -11.15) * mm});
            skLineSegment(sketch, "E23.2.4.0", {"start": v(-85.83, -23.85) * mm, "end": v(-90.45, -23.85) * mm});
            skLineSegment(sketch, "E23.2.4.1", {"start": v(-85.83, -28.47) * mm, "end": v(-85.83, -23.85) * mm});
            skLineSegment(sketch, "E23.2.4.2", {"start": v(-85.83, -28.47) * mm, "end": v(-90.45, -28.47) * mm});
            skLineSegment(sketch, "E23.2.4.3", {"start": v(-90.45, -28.47) * mm, "end": v(-90.45, -23.85) * mm});
            skLineSegment(sketch, "E23.3.0.0", {"start": v(-73.13, 26.95) * mm, "end": v(-77.75, 26.95) * mm});
            skLineSegment(sketch, "E23.3.0.1", {"start": v(-73.13, 22.33) * mm, "end": v(-73.13, 26.95) * mm});
            skLineSegment(sketch, "E23.3.0.2", {"start": v(-73.13, 22.33) * mm, "end": v(-77.75, 22.33) * mm});
            skLineSegment(sketch, "E23.3.0.3", {"start": v(-77.75, 22.33) * mm, "end": v(-77.75, 26.95) * mm});
            skLineSegment(sketch, "E23.3.1.0", {"start": v(-73.13, 14.25) * mm, "end": v(-77.75, 14.25) * mm});
            skLineSegment(sketch, "E23.3.1.1", {"start": v(-73.13, 9.63) * mm, "end": v(-73.13, 14.25) * mm});
            skLineSegment(sketch, "E23.3.1.2", {"start": v(-73.13, 9.63) * mm, "end": v(-77.75, 9.63) * mm});
            skLineSegment(sketch, "E23.3.1.3", {"start": v(-77.75, 9.63) * mm, "end": v(-77.75, 14.25) * mm});
            skLineSegment(sketch, "E23.3.2.0", {"start": v(-73.13, 1.55) * mm, "end": v(-77.75, 1.55) * mm});
            skLineSegment(sketch, "E23.3.2.1", {"start": v(-73.13, -3.07) * mm, "end": v(-73.13, 1.55) * mm});
            skLineSegment(sketch, "E23.3.2.2", {"start": v(-73.13, -3.07) * mm, "end": v(-77.75, -3.07) * mm});
            skLineSegment(sketch, "E23.3.2.3", {"start": v(-77.75, -3.07) * mm, "end": v(-77.75, 1.55) * mm});
            skLineSegment(sketch, "E23.3.3.0", {"start": v(-73.13, -11.15) * mm, "end": v(-77.75, -11.15) * mm});
            skLineSegment(sketch, "E23.3.3.1", {"start": v(-73.13, -15.77) * mm, "end": v(-73.13, -11.15) * mm});
            skLineSegment(sketch, "E23.3.3.2", {"start": v(-73.13, -15.77) * mm, "end": v(-77.75, -15.77) * mm});
            skLineSegment(sketch, "E23.3.3.3", {"start": v(-77.75, -15.77) * mm, "end": v(-77.75, -11.15) * mm});
            skLineSegment(sketch, "E23.3.4.0", {"start": v(-73.13, -23.85) * mm, "end": v(-77.75, -23.85) * mm});
            skLineSegment(sketch, "E23.3.4.1", {"start": v(-73.13, -28.47) * mm, "end": v(-73.13, -23.85) * mm});
            skLineSegment(sketch, "E23.3.4.2", {"start": v(-73.13, -28.47) * mm, "end": v(-77.75, -28.47) * mm});
            skLineSegment(sketch, "E23.3.4.3", {"start": v(-77.75, -28.47) * mm, "end": v(-77.75, -23.85) * mm});
            skLineSegment(sketch, "E23.4.0.0", {"start": v(-60.43, 26.95) * mm, "end": v(-65.05, 26.95) * mm});
            skLineSegment(sketch, "E23.4.0.1", {"start": v(-60.43, 22.33) * mm, "end": v(-60.43, 26.95) * mm});
            skLineSegment(sketch, "E23.4.0.2", {"start": v(-60.43, 22.33) * mm, "end": v(-65.05, 22.33) * mm});
            skLineSegment(sketch, "E23.4.0.3", {"start": v(-65.05, 22.33) * mm, "end": v(-65.05, 26.95) * mm});
            skLineSegment(sketch, "E23.4.1.0", {"start": v(-60.43, 14.25) * mm, "end": v(-65.05, 14.25) * mm});
            skLineSegment(sketch, "E23.4.1.1", {"start": v(-60.43, 9.63) * mm, "end": v(-60.43, 14.25) * mm});
            skLineSegment(sketch, "E23.4.1.2", {"start": v(-60.43, 9.63) * mm, "end": v(-65.05, 9.63) * mm});
            skLineSegment(sketch, "E23.4.1.3", {"start": v(-65.05, 9.63) * mm, "end": v(-65.05, 14.25) * mm});
            skLineSegment(sketch, "E23.4.2.0", {"start": v(-60.43, 1.55) * mm, "end": v(-65.05, 1.55) * mm});
            skLineSegment(sketch, "E23.4.2.1", {"start": v(-60.43, -3.07) * mm, "end": v(-60.43, 1.55) * mm});
            skLineSegment(sketch, "E23.4.2.2", {"start": v(-60.43, -3.07) * mm, "end": v(-65.05, -3.07) * mm});
            skLineSegment(sketch, "E23.4.2.3", {"start": v(-65.05, -3.07) * mm, "end": v(-65.05, 1.55) * mm});
            skLineSegment(sketch, "E23.4.3.0", {"start": v(-60.43, -11.15) * mm, "end": v(-65.05, -11.15) * mm});
            skLineSegment(sketch, "E23.4.3.1", {"start": v(-60.43, -15.77) * mm, "end": v(-60.43, -11.15) * mm});
            skLineSegment(sketch, "E23.4.3.2", {"start": v(-60.43, -15.77) * mm, "end": v(-65.05, -15.77) * mm});
            skLineSegment(sketch, "E23.4.3.3", {"start": v(-65.05, -15.77) * mm, "end": v(-65.05, -11.15) * mm});
            skLineSegment(sketch, "E23.4.4.0", {"start": v(-60.43, -23.85) * mm, "end": v(-65.05, -23.85) * mm});
            skLineSegment(sketch, "E23.4.4.1", {"start": v(-60.43, -28.47) * mm, "end": v(-60.43, -23.85) * mm});
            skLineSegment(sketch, "E23.4.4.2", {"start": v(-60.43, -28.47) * mm, "end": v(-65.05, -28.47) * mm});
            skLineSegment(sketch, "E23.4.4.3", {"start": v(-65.05, -28.47) * mm, "end": v(-65.05, -23.85) * mm});
            skLineSegment(sketch, "E23.5.0.0", {"start": v(-47.73, 26.95) * mm, "end": v(-52.35, 26.95) * mm});
            skLineSegment(sketch, "E23.5.0.1", {"start": v(-47.73, 22.33) * mm, "end": v(-47.73, 26.95) * mm});
            skLineSegment(sketch, "E23.5.0.2", {"start": v(-47.73, 22.33) * mm, "end": v(-52.35, 22.33) * mm});
            skLineSegment(sketch, "E23.5.0.3", {"start": v(-52.35, 22.33) * mm, "end": v(-52.35, 26.95) * mm});
            skLineSegment(sketch, "E23.5.1.0", {"start": v(-47.73, 14.25) * mm, "end": v(-52.35, 14.25) * mm});
            skLineSegment(sketch, "E23.5.1.1", {"start": v(-47.73, 9.63) * mm, "end": v(-47.73, 14.25) * mm});
            skLineSegment(sketch, "E23.5.1.2", {"start": v(-47.73, 9.63) * mm, "end": v(-52.35, 9.63) * mm});
            skLineSegment(sketch, "E23.5.1.3", {"start": v(-52.35, 9.63) * mm, "end": v(-52.35, 14.25) * mm});
            skLineSegment(sketch, "E23.5.2.0", {"start": v(-47.73, 1.55) * mm, "end": v(-52.35, 1.55) * mm});
            skLineSegment(sketch, "E23.5.2.1", {"start": v(-47.73, -3.07) * mm, "end": v(-47.73, 1.55) * mm});
            skLineSegment(sketch, "E23.5.2.2", {"start": v(-47.73, -3.07) * mm, "end": v(-52.35, -3.07) * mm});
            skLineSegment(sketch, "E23.5.2.3", {"start": v(-52.35, -3.07) * mm, "end": v(-52.35, 1.55) * mm});
            skLineSegment(sketch, "E23.5.3.0", {"start": v(-47.73, -11.15) * mm, "end": v(-52.35, -11.15) * mm});
            skLineSegment(sketch, "E23.5.3.1", {"start": v(-47.73, -15.77) * mm, "end": v(-47.73, -11.15) * mm});
            skLineSegment(sketch, "E23.5.3.2", {"start": v(-47.73, -15.77) * mm, "end": v(-52.35, -15.77) * mm});
            skLineSegment(sketch, "E23.5.3.3", {"start": v(-52.35, -15.77) * mm, "end": v(-52.35, -11.15) * mm});
            skLineSegment(sketch, "E23.5.4.0", {"start": v(-47.73, -23.85) * mm, "end": v(-52.35, -23.85) * mm});
            skLineSegment(sketch, "E23.5.4.1", {"start": v(-47.73, -28.47) * mm, "end": v(-47.73, -23.85) * mm});
            skLineSegment(sketch, "E23.5.4.2", {"start": v(-47.73, -28.47) * mm, "end": v(-52.35, -28.47) * mm});
            skLineSegment(sketch, "E23.5.4.3", {"start": v(-52.35, -28.47) * mm, "end": v(-52.35, -23.85) * mm});
            skLineSegment(sketch, "E23.6.0.0", {"start": v(-35.03, 26.95) * mm, "end": v(-39.65, 26.95) * mm});
            skLineSegment(sketch, "E23.6.0.1", {"start": v(-35.03, 22.33) * mm, "end": v(-35.03, 26.95) * mm});
            skLineSegment(sketch, "E23.6.0.2", {"start": v(-35.03, 22.33) * mm, "end": v(-39.65, 22.33) * mm});
            skLineSegment(sketch, "E23.6.0.3", {"start": v(-39.65, 22.33) * mm, "end": v(-39.65, 26.95) * mm});
            skLineSegment(sketch, "E23.6.1.0", {"start": v(-35.03, 14.25) * mm, "end": v(-39.65, 14.25) * mm});
            skLineSegment(sketch, "E23.6.1.1", {"start": v(-35.03, 9.63) * mm, "end": v(-35.03, 14.25) * mm});
            skLineSegment(sketch, "E23.6.1.2", {"start": v(-35.03, 9.63) * mm, "end": v(-39.65, 9.63) * mm});
            skLineSegment(sketch, "E23.6.1.3", {"start": v(-39.65, 9.63) * mm, "end": v(-39.65, 14.25) * mm});
            skLineSegment(sketch, "E23.6.2.0", {"start": v(-35.03, 1.55) * mm, "end": v(-39.65, 1.55) * mm});
            skLineSegment(sketch, "E23.6.2.1", {"start": v(-35.03, -3.07) * mm, "end": v(-35.03, 1.55) * mm});
            skLineSegment(sketch, "E23.6.2.2", {"start": v(-35.03, -3.07) * mm, "end": v(-39.65, -3.07) * mm});
            skLineSegment(sketch, "E23.6.2.3", {"start": v(-39.65, -3.07) * mm, "end": v(-39.65, 1.55) * mm});
            skLineSegment(sketch, "E23.6.3.0", {"start": v(-35.03, -11.15) * mm, "end": v(-39.65, -11.15) * mm});
            skLineSegment(sketch, "E23.6.3.1", {"start": v(-35.03, -15.77) * mm, "end": v(-35.03, -11.15) * mm});
            skLineSegment(sketch, "E23.6.3.2", {"start": v(-35.03, -15.77) * mm, "end": v(-39.65, -15.77) * mm});
            skLineSegment(sketch, "E23.6.3.3", {"start": v(-39.65, -15.77) * mm, "end": v(-39.65, -11.15) * mm});
            skLineSegment(sketch, "E23.6.4.0", {"start": v(-35.03, -23.85) * mm, "end": v(-39.65, -23.85) * mm});
            skLineSegment(sketch, "E23.6.4.1", {"start": v(-35.03, -28.47) * mm, "end": v(-35.03, -23.85) * mm});
            skLineSegment(sketch, "E23.6.4.2", {"start": v(-35.03, -28.47) * mm, "end": v(-39.65, -28.47) * mm});
            skLineSegment(sketch, "E23.6.4.3", {"start": v(-39.65, -28.47) * mm, "end": v(-39.65, -23.85) * mm});
            skLineSegment(sketch, "E23.7.0.0", {"start": v(-22.33, 26.95) * mm, "end": v(-26.95, 26.95) * mm});
            skLineSegment(sketch, "E23.7.0.1", {"start": v(-22.33, 22.33) * mm, "end": v(-22.33, 26.95) * mm});
            skLineSegment(sketch, "E23.7.0.2", {"start": v(-22.33, 22.33) * mm, "end": v(-26.95, 22.33) * mm});
            skLineSegment(sketch, "E23.7.0.3", {"start": v(-26.95, 22.33) * mm, "end": v(-26.95, 26.95) * mm});
            skLineSegment(sketch, "E23.7.1.0", {"start": v(-22.33, 14.25) * mm, "end": v(-26.95, 14.25) * mm});
            skLineSegment(sketch, "E23.7.1.1", {"start": v(-22.33, 9.63) * mm, "end": v(-22.33, 14.25) * mm});
            skLineSegment(sketch, "E23.7.1.2", {"start": v(-22.33, 9.63) * mm, "end": v(-26.95, 9.63) * mm});
            skLineSegment(sketch, "E23.7.1.3", {"start": v(-26.95, 9.63) * mm, "end": v(-26.95, 14.25) * mm});
            skLineSegment(sketch, "E23.7.2.0", {"start": v(-22.33, 1.55) * mm, "end": v(-26.95, 1.55) * mm});
            skLineSegment(sketch, "E23.7.2.1", {"start": v(-22.33, -3.07) * mm, "end": v(-22.33, 1.55) * mm});
            skLineSegment(sketch, "E23.7.2.2", {"start": v(-22.33, -3.07) * mm, "end": v(-26.95, -3.07) * mm});
            skLineSegment(sketch, "E23.7.2.3", {"start": v(-26.95, -3.07) * mm, "end": v(-26.95, 1.55) * mm});
            skLineSegment(sketch, "E23.7.3.0", {"start": v(-22.33, -11.15) * mm, "end": v(-26.95, -11.15) * mm});
            skLineSegment(sketch, "E23.7.3.1", {"start": v(-22.33, -15.77) * mm, "end": v(-22.33, -11.15) * mm});
            skLineSegment(sketch, "E23.7.3.2", {"start": v(-22.33, -15.77) * mm, "end": v(-26.95, -15.77) * mm});
            skLineSegment(sketch, "E23.7.3.3", {"start": v(-26.95, -15.77) * mm, "end": v(-26.95, -11.15) * mm});
            skLineSegment(sketch, "E23.7.4.0", {"start": v(-22.33, -23.85) * mm, "end": v(-26.95, -23.85) * mm});
            skLineSegment(sketch, "E23.7.4.1", {"start": v(-22.33, -28.47) * mm, "end": v(-22.33, -23.85) * mm});
            skLineSegment(sketch, "E23.7.4.2", {"start": v(-22.33, -28.47) * mm, "end": v(-26.95, -28.47) * mm});
            skLineSegment(sketch, "E23.7.4.3", {"start": v(-26.95, -28.47) * mm, "end": v(-26.95, -23.85) * mm});
            skLineSegment(sketch, "E23.8.0.0", {"start": v(-9.63, 26.95) * mm, "end": v(-14.25, 26.95) * mm});
            skLineSegment(sketch, "E23.8.0.1", {"start": v(-9.63, 22.33) * mm, "end": v(-9.63, 26.95) * mm});
            skLineSegment(sketch, "E23.8.0.2", {"start": v(-9.63, 22.33) * mm, "end": v(-14.25, 22.33) * mm});
            skLineSegment(sketch, "E23.8.0.3", {"start": v(-14.25, 22.33) * mm, "end": v(-14.25, 26.95) * mm});
            skLineSegment(sketch, "E23.8.1.0", {"start": v(-9.63, 14.25) * mm, "end": v(-14.25, 14.25) * mm});
            skLineSegment(sketch, "E23.8.1.1", {"start": v(-9.63, 9.63) * mm, "end": v(-9.63, 14.25) * mm});
            skLineSegment(sketch, "E23.8.1.2", {"start": v(-9.63, 9.63) * mm, "end": v(-14.25, 9.63) * mm});
            skLineSegment(sketch, "E23.8.1.3", {"start": v(-14.25, 9.63) * mm, "end": v(-14.25, 14.25) * mm});
            skLineSegment(sketch, "E23.8.2.0", {"start": v(-9.63, 1.55) * mm, "end": v(-14.25, 1.55) * mm});
            skLineSegment(sketch, "E23.8.2.1", {"start": v(-9.63, -3.07) * mm, "end": v(-9.63, 1.55) * mm});
            skLineSegment(sketch, "E23.8.2.2", {"start": v(-9.63, -3.07) * mm, "end": v(-14.25, -3.07) * mm});
            skLineSegment(sketch, "E23.8.2.3", {"start": v(-14.25, -3.07) * mm, "end": v(-14.25, 1.55) * mm});
            skLineSegment(sketch, "E23.8.3.0", {"start": v(-9.63, -11.15) * mm, "end": v(-14.25, -11.15) * mm});
            skLineSegment(sketch, "E23.8.3.1", {"start": v(-9.63, -15.77) * mm, "end": v(-9.63, -11.15) * mm});
            skLineSegment(sketch, "E23.8.3.2", {"start": v(-9.63, -15.77) * mm, "end": v(-14.25, -15.77) * mm});
            skLineSegment(sketch, "E23.8.3.3", {"start": v(-14.25, -15.77) * mm, "end": v(-14.25, -11.15) * mm});
            skLineSegment(sketch, "E23.8.4.0", {"start": v(-9.63, -23.85) * mm, "end": v(-14.25, -23.85) * mm});
            skLineSegment(sketch, "E23.8.4.1", {"start": v(-9.63, -28.47) * mm, "end": v(-9.63, -23.85) * mm});
            skLineSegment(sketch, "E23.8.4.2", {"start": v(-9.63, -28.47) * mm, "end": v(-14.25, -28.47) * mm});
            skLineSegment(sketch, "E23.8.4.3", {"start": v(-14.25, -28.47) * mm, "end": v(-14.25, -23.85) * mm});
            skLineSegment(sketch, "E23.9.0.0", {"start": v(3.07, 26.95) * mm, "end": v(-1.55, 26.95) * mm});
            skLineSegment(sketch, "E23.9.0.1", {"start": v(3.07, 22.33) * mm, "end": v(3.07, 26.95) * mm});
            skLineSegment(sketch, "E23.9.0.2", {"start": v(3.07, 22.33) * mm, "end": v(-1.55, 22.33) * mm});
            skLineSegment(sketch, "E23.9.0.3", {"start": v(-1.55, 22.33) * mm, "end": v(-1.55, 26.95) * mm});
            skLineSegment(sketch, "E23.9.1.0", {"start": v(3.07, 14.25) * mm, "end": v(-1.55, 14.25) * mm});
            skLineSegment(sketch, "E23.9.1.1", {"start": v(3.07, 9.63) * mm, "end": v(3.07, 14.25) * mm});
            skLineSegment(sketch, "E23.9.1.2", {"start": v(3.07, 9.63) * mm, "end": v(-1.55, 9.63) * mm});
            skLineSegment(sketch, "E23.9.1.3", {"start": v(-1.55, 9.63) * mm, "end": v(-1.55, 14.25) * mm});
            skLineSegment(sketch, "E23.9.2.0", {"start": v(3.07, 1.55) * mm, "end": v(-1.55, 1.55) * mm});
            skLineSegment(sketch, "E23.9.2.1", {"start": v(3.07, -3.07) * mm, "end": v(3.07, 1.55) * mm});
            skLineSegment(sketch, "E23.9.2.2", {"start": v(3.07, -3.07) * mm, "end": v(-1.55, -3.07) * mm});
            skLineSegment(sketch, "E23.9.2.3", {"start": v(-1.55, -3.07) * mm, "end": v(-1.55, 1.55) * mm});
            skLineSegment(sketch, "E23.9.3.0", {"start": v(3.07, -11.15) * mm, "end": v(-1.55, -11.15) * mm});
            skLineSegment(sketch, "E23.9.3.1", {"start": v(3.07, -15.77) * mm, "end": v(3.07, -11.15) * mm});
            skLineSegment(sketch, "E23.9.3.2", {"start": v(3.07, -15.77) * mm, "end": v(-1.55, -15.77) * mm});
            skLineSegment(sketch, "E23.9.3.3", {"start": v(-1.55, -15.77) * mm, "end": v(-1.55, -11.15) * mm});
            skLineSegment(sketch, "E23.9.4.0", {"start": v(3.07, -23.85) * mm, "end": v(-1.55, -23.85) * mm});
            skLineSegment(sketch, "E23.9.4.1", {"start": v(3.07, -28.47) * mm, "end": v(3.07, -23.85) * mm});
            skLineSegment(sketch, "E23.9.4.2", {"start": v(3.07, -28.47) * mm, "end": v(-1.55, -28.47) * mm});
            skLineSegment(sketch, "E23.9.4.3", {"start": v(-1.55, -28.47) * mm, "end": v(-1.55, -23.85) * mm});
            skLineSegment(sketch, "E23.10.0.0", {"start": v(15.77, 26.95) * mm, "end": v(11.15, 26.95) * mm});
            skLineSegment(sketch, "E23.10.0.1", {"start": v(15.77, 22.33) * mm, "end": v(15.77, 26.95) * mm});
            skLineSegment(sketch, "E23.10.0.2", {"start": v(15.77, 22.33) * mm, "end": v(11.15, 22.33) * mm});
            skLineSegment(sketch, "E23.10.0.3", {"start": v(11.15, 22.33) * mm, "end": v(11.15, 26.95) * mm});
            skLineSegment(sketch, "E23.10.1.0", {"start": v(15.77, 14.25) * mm, "end": v(11.15, 14.25) * mm});
            skLineSegment(sketch, "E23.10.1.1", {"start": v(15.77, 9.63) * mm, "end": v(15.77, 14.25) * mm});
            skLineSegment(sketch, "E23.10.1.2", {"start": v(15.77, 9.63) * mm, "end": v(11.15, 9.63) * mm});
            skLineSegment(sketch, "E23.10.1.3", {"start": v(11.15, 9.63) * mm, "end": v(11.15, 14.25) * mm});
            skLineSegment(sketch, "E23.10.2.0", {"start": v(15.77, 1.55) * mm, "end": v(11.15, 1.55) * mm});
            skLineSegment(sketch, "E23.10.2.1", {"start": v(15.77, -3.07) * mm, "end": v(15.77, 1.55) * mm});
            skLineSegment(sketch, "E23.10.2.2", {"start": v(15.77, -3.07) * mm, "end": v(11.15, -3.07) * mm});
            skLineSegment(sketch, "E23.10.2.3", {"start": v(11.15, -3.07) * mm, "end": v(11.15, 1.55) * mm});
            skLineSegment(sketch, "E23.10.3.0", {"start": v(15.77, -11.15) * mm, "end": v(11.15, -11.15) * mm});
            skLineSegment(sketch, "E23.10.3.1", {"start": v(15.77, -15.77) * mm, "end": v(15.77, -11.15) * mm});
            skLineSegment(sketch, "E23.10.3.2", {"start": v(15.77, -15.77) * mm, "end": v(11.15, -15.77) * mm});
            skLineSegment(sketch, "E23.10.3.3", {"start": v(11.15, -15.77) * mm, "end": v(11.15, -11.15) * mm});
            skLineSegment(sketch, "E23.10.4.0", {"start": v(15.77, -23.85) * mm, "end": v(11.15, -23.85) * mm});
            skLineSegment(sketch, "E23.10.4.1", {"start": v(15.77, -28.47) * mm, "end": v(15.77, -23.85) * mm});
            skLineSegment(sketch, "E23.10.4.2", {"start": v(15.77, -28.47) * mm, "end": v(11.15, -28.47) * mm});
            skLineSegment(sketch, "E23.10.4.3", {"start": v(11.15, -28.47) * mm, "end": v(11.15, -23.85) * mm});
            skLineSegment(sketch, "E23.11.0.0", {"start": v(28.47, 26.95) * mm, "end": v(23.85, 26.95) * mm});
            skLineSegment(sketch, "E23.11.0.1", {"start": v(28.47, 22.33) * mm, "end": v(28.47, 26.95) * mm});
            skLineSegment(sketch, "E23.11.0.2", {"start": v(28.47, 22.33) * mm, "end": v(23.85, 22.33) * mm});
            skLineSegment(sketch, "E23.11.0.3", {"start": v(23.85, 22.33) * mm, "end": v(23.85, 26.95) * mm});
            skLineSegment(sketch, "E23.11.1.0", {"start": v(28.47, 14.25) * mm, "end": v(23.85, 14.25) * mm});
            skLineSegment(sketch, "E23.11.1.1", {"start": v(28.47, 9.63) * mm, "end": v(28.47, 14.25) * mm});
            skLineSegment(sketch, "E23.11.1.2", {"start": v(28.47, 9.63) * mm, "end": v(23.85, 9.63) * mm});
            skLineSegment(sketch, "E23.11.1.3", {"start": v(23.85, 9.63) * mm, "end": v(23.85, 14.25) * mm});
            skLineSegment(sketch, "E23.11.2.0", {"start": v(28.47, 1.55) * mm, "end": v(23.85, 1.55) * mm});
            skLineSegment(sketch, "E23.11.2.1", {"start": v(28.47, -3.07) * mm, "end": v(28.47, 1.55) * mm});
            skLineSegment(sketch, "E23.11.2.2", {"start": v(28.47, -3.07) * mm, "end": v(23.85, -3.07) * mm});
            skLineSegment(sketch, "E23.11.2.3", {"start": v(23.85, -3.07) * mm, "end": v(23.85, 1.55) * mm});
            skLineSegment(sketch, "E23.11.3.0", {"start": v(28.47, -11.15) * mm, "end": v(23.85, -11.15) * mm});
            skLineSegment(sketch, "E23.11.3.1", {"start": v(28.47, -15.77) * mm, "end": v(28.47, -11.15) * mm});
            skLineSegment(sketch, "E23.11.3.2", {"start": v(28.47, -15.77) * mm, "end": v(23.85, -15.77) * mm});
            skLineSegment(sketch, "E23.11.3.3", {"start": v(23.85, -15.77) * mm, "end": v(23.85, -11.15) * mm});
            skLineSegment(sketch, "E23.11.4.0", {"start": v(28.47, -23.85) * mm, "end": v(23.85, -23.85) * mm});
            skLineSegment(sketch, "E23.11.4.1", {"start": v(28.47, -28.47) * mm, "end": v(28.47, -23.85) * mm});
            skLineSegment(sketch, "E23.11.4.2", {"start": v(28.47, -28.47) * mm, "end": v(23.85, -28.47) * mm});
            skLineSegment(sketch, "E23.11.4.3", {"start": v(23.85, -28.47) * mm, "end": v(23.85, -23.85) * mm});
            skLineSegment(sketch, "E23.12.0.0", {"start": v(41.17, 26.95) * mm, "end": v(36.55, 26.95) * mm});
            skLineSegment(sketch, "E23.12.0.1", {"start": v(41.17, 22.33) * mm, "end": v(41.17, 26.95) * mm});
            skLineSegment(sketch, "E23.12.0.2", {"start": v(41.17, 22.33) * mm, "end": v(36.55, 22.33) * mm});
            skLineSegment(sketch, "E23.12.0.3", {"start": v(36.55, 22.33) * mm, "end": v(36.55, 26.95) * mm});
            skLineSegment(sketch, "E23.12.1.0", {"start": v(41.17, 14.25) * mm, "end": v(36.55, 14.25) * mm});
            skLineSegment(sketch, "E23.12.1.1", {"start": v(41.17, 9.63) * mm, "end": v(41.17, 14.25) * mm});
            skLineSegment(sketch, "E23.12.1.2", {"start": v(41.17, 9.63) * mm, "end": v(36.55, 9.63) * mm});
            skLineSegment(sketch, "E23.12.1.3", {"start": v(36.55, 9.63) * mm, "end": v(36.55, 14.25) * mm});
            skLineSegment(sketch, "E23.12.2.0", {"start": v(41.17, 1.55) * mm, "end": v(36.55, 1.55) * mm});
            skLineSegment(sketch, "E23.12.2.1", {"start": v(41.17, -3.07) * mm, "end": v(41.17, 1.55) * mm});
            skLineSegment(sketch, "E23.12.2.2", {"start": v(41.17, -3.07) * mm, "end": v(36.55, -3.07) * mm});
            skLineSegment(sketch, "E23.12.2.3", {"start": v(36.55, -3.07) * mm, "end": v(36.55, 1.55) * mm});
            skLineSegment(sketch, "E23.12.3.0", {"start": v(41.17, -11.15) * mm, "end": v(36.55, -11.15) * mm});
            skLineSegment(sketch, "E23.12.3.1", {"start": v(41.17, -15.77) * mm, "end": v(41.17, -11.15) * mm});
            skLineSegment(sketch, "E23.12.3.2", {"start": v(41.17, -15.77) * mm, "end": v(36.55, -15.77) * mm});
            skLineSegment(sketch, "E23.12.3.3", {"start": v(36.55, -15.77) * mm, "end": v(36.55, -11.15) * mm});
            skLineSegment(sketch, "E23.12.4.0", {"start": v(41.17, -23.85) * mm, "end": v(36.55, -23.85) * mm});
            skLineSegment(sketch, "E23.12.4.1", {"start": v(41.17, -28.47) * mm, "end": v(41.17, -23.85) * mm});
            skLineSegment(sketch, "E23.12.4.2", {"start": v(41.17, -28.47) * mm, "end": v(36.55, -28.47) * mm});
            skLineSegment(sketch, "E23.12.4.3", {"start": v(36.55, -28.47) * mm, "end": v(36.55, -23.85) * mm});
            skLineSegment(sketch, "E23.13.0.0", {"start": v(53.87, 26.95) * mm, "end": v(49.25, 26.95) * mm});
            skLineSegment(sketch, "E23.13.0.1", {"start": v(53.87, 22.33) * mm, "end": v(53.87, 26.95) * mm});
            skLineSegment(sketch, "E23.13.0.2", {"start": v(53.87, 22.33) * mm, "end": v(49.25, 22.33) * mm});
            skLineSegment(sketch, "E23.13.0.3", {"start": v(49.25, 22.33) * mm, "end": v(49.25, 26.95) * mm});
            skLineSegment(sketch, "E23.13.1.0", {"start": v(53.87, 14.25) * mm, "end": v(49.25, 14.25) * mm});
            skLineSegment(sketch, "E23.13.1.1", {"start": v(53.87, 9.63) * mm, "end": v(53.87, 14.25) * mm});
            skLineSegment(sketch, "E23.13.1.2", {"start": v(53.87, 9.63) * mm, "end": v(49.25, 9.63) * mm});
            skLineSegment(sketch, "E23.13.1.3", {"start": v(49.25, 9.63) * mm, "end": v(49.25, 14.25) * mm});
            skLineSegment(sketch, "E23.13.2.0", {"start": v(53.87, 1.55) * mm, "end": v(49.25, 1.55) * mm});
            skLineSegment(sketch, "E23.13.2.1", {"start": v(53.87, -3.07) * mm, "end": v(53.87, 1.55) * mm});
            skLineSegment(sketch, "E23.13.2.2", {"start": v(53.87, -3.07) * mm, "end": v(49.25, -3.07) * mm});
            skLineSegment(sketch, "E23.13.2.3", {"start": v(49.25, -3.07) * mm, "end": v(49.25, 1.55) * mm});
            skLineSegment(sketch, "E23.13.3.0", {"start": v(53.87, -11.15) * mm, "end": v(49.25, -11.15) * mm});
            skLineSegment(sketch, "E23.13.3.1", {"start": v(53.87, -15.77) * mm, "end": v(53.87, -11.15) * mm});
            skLineSegment(sketch, "E23.13.3.2", {"start": v(53.87, -15.77) * mm, "end": v(49.25, -15.77) * mm});
            skLineSegment(sketch, "E23.13.3.3", {"start": v(49.25, -15.77) * mm, "end": v(49.25, -11.15) * mm});
            skLineSegment(sketch, "E23.13.4.0", {"start": v(53.87, -23.85) * mm, "end": v(49.25, -23.85) * mm});
            skLineSegment(sketch, "E23.13.4.1", {"start": v(53.87, -28.47) * mm, "end": v(53.87, -23.85) * mm});
            skLineSegment(sketch, "E23.13.4.2", {"start": v(53.87, -28.47) * mm, "end": v(49.25, -28.47) * mm});
            skLineSegment(sketch, "E23.13.4.3", {"start": v(49.25, -28.47) * mm, "end": v(49.25, -23.85) * mm});
            skLineSegment(sketch, "E23.14.0.0", {"start": v(66.57, 26.95) * mm, "end": v(61.95, 26.95) * mm});
            skLineSegment(sketch, "E23.14.0.1", {"start": v(66.57, 22.33) * mm, "end": v(66.57, 26.95) * mm});
            skLineSegment(sketch, "E23.14.0.2", {"start": v(66.57, 22.33) * mm, "end": v(61.95, 22.33) * mm});
            skLineSegment(sketch, "E23.14.0.3", {"start": v(61.95, 22.33) * mm, "end": v(61.95, 26.95) * mm});
            skLineSegment(sketch, "E23.14.1.0", {"start": v(66.57, 14.25) * mm, "end": v(61.95, 14.25) * mm});
            skLineSegment(sketch, "E23.14.1.1", {"start": v(66.57, 9.63) * mm, "end": v(66.57, 14.25) * mm});
            skLineSegment(sketch, "E23.14.1.2", {"start": v(66.57, 9.63) * mm, "end": v(61.95, 9.63) * mm});
            skLineSegment(sketch, "E23.14.1.3", {"start": v(61.95, 9.63) * mm, "end": v(61.95, 14.25) * mm});
            skLineSegment(sketch, "E23.14.2.0", {"start": v(66.57, 1.55) * mm, "end": v(61.95, 1.55) * mm});
            skLineSegment(sketch, "E23.14.2.1", {"start": v(66.57, -3.07) * mm, "end": v(66.57, 1.55) * mm});
            skLineSegment(sketch, "E23.14.2.2", {"start": v(66.57, -3.07) * mm, "end": v(61.95, -3.07) * mm});
            skLineSegment(sketch, "E23.14.2.3", {"start": v(61.95, -3.07) * mm, "end": v(61.95, 1.55) * mm});
            skLineSegment(sketch, "E23.14.3.0", {"start": v(66.57, -11.15) * mm, "end": v(61.95, -11.15) * mm});
            skLineSegment(sketch, "E23.14.3.1", {"start": v(66.57, -15.77) * mm, "end": v(66.57, -11.15) * mm});
            skLineSegment(sketch, "E23.14.3.2", {"start": v(66.57, -15.77) * mm, "end": v(61.95, -15.77) * mm});
            skLineSegment(sketch, "E23.14.3.3", {"start": v(61.95, -15.77) * mm, "end": v(61.95, -11.15) * mm});
            skLineSegment(sketch, "E23.14.4.0", {"start": v(66.57, -23.85) * mm, "end": v(61.95, -23.85) * mm});
            skLineSegment(sketch, "E23.14.4.1", {"start": v(66.57, -28.47) * mm, "end": v(66.57, -23.85) * mm});
            skLineSegment(sketch, "E23.14.4.2", {"start": v(66.57, -28.47) * mm, "end": v(61.95, -28.47) * mm});
            skLineSegment(sketch, "E23.14.4.3", {"start": v(61.95, -28.47) * mm, "end": v(61.95, -23.85) * mm});
            skLineSegment(sketch, "E23.15.0.0", {"start": v(79.27, 26.95) * mm, "end": v(74.65, 26.95) * mm});
            skLineSegment(sketch, "E23.15.0.1", {"start": v(79.27, 22.33) * mm, "end": v(79.27, 26.95) * mm});
            skLineSegment(sketch, "E23.15.0.2", {"start": v(79.27, 22.33) * mm, "end": v(74.65, 22.33) * mm});
            skLineSegment(sketch, "E23.15.0.3", {"start": v(74.65, 22.33) * mm, "end": v(74.65, 26.95) * mm});
            skLineSegment(sketch, "E23.15.1.0", {"start": v(79.27, 14.25) * mm, "end": v(74.65, 14.25) * mm});
            skLineSegment(sketch, "E23.15.1.1", {"start": v(79.27, 9.63) * mm, "end": v(79.27, 14.25) * mm});
            skLineSegment(sketch, "E23.15.1.2", {"start": v(79.27, 9.63) * mm, "end": v(74.65, 9.63) * mm});
            skLineSegment(sketch, "E23.15.1.3", {"start": v(74.65, 9.63) * mm, "end": v(74.65, 14.25) * mm});
            skLineSegment(sketch, "E23.15.2.0", {"start": v(79.27, 1.55) * mm, "end": v(74.65, 1.55) * mm});
            skLineSegment(sketch, "E23.15.2.1", {"start": v(79.27, -3.07) * mm, "end": v(79.27, 1.55) * mm});
            skLineSegment(sketch, "E23.15.2.2", {"start": v(79.27, -3.07) * mm, "end": v(74.65, -3.07) * mm});
            skLineSegment(sketch, "E23.15.2.3", {"start": v(74.65, -3.07) * mm, "end": v(74.65, 1.55) * mm});
            skLineSegment(sketch, "E23.15.3.0", {"start": v(79.27, -11.15) * mm, "end": v(74.65, -11.15) * mm});
            skLineSegment(sketch, "E23.15.3.1", {"start": v(79.27, -15.77) * mm, "end": v(79.27, -11.15) * mm});
            skLineSegment(sketch, "E23.15.3.2", {"start": v(79.27, -15.77) * mm, "end": v(74.65, -15.77) * mm});
            skLineSegment(sketch, "E23.15.3.3", {"start": v(74.65, -15.77) * mm, "end": v(74.65, -11.15) * mm});
            skLineSegment(sketch, "E23.15.4.0", {"start": v(79.27, -23.85) * mm, "end": v(74.65, -23.85) * mm});
            skLineSegment(sketch, "E23.15.4.1", {"start": v(79.27, -28.47) * mm, "end": v(79.27, -23.85) * mm});
            skLineSegment(sketch, "E23.15.4.2", {"start": v(79.27, -28.47) * mm, "end": v(74.65, -28.47) * mm});
            skLineSegment(sketch, "E23.15.4.3", {"start": v(74.65, -28.47) * mm, "end": v(74.65, -23.85) * mm});
            skLineSegment(sketch, "E23.16.0.0", {"start": v(91.97, 26.95) * mm, "end": v(87.35, 26.95) * mm});
            skLineSegment(sketch, "E23.16.0.1", {"start": v(91.97, 22.33) * mm, "end": v(91.97, 26.95) * mm});
            skLineSegment(sketch, "E23.16.0.2", {"start": v(91.97, 22.33) * mm, "end": v(87.35, 22.33) * mm});
            skLineSegment(sketch, "E23.16.0.3", {"start": v(87.35, 22.33) * mm, "end": v(87.35, 26.95) * mm});
            skLineSegment(sketch, "E23.16.1.0", {"start": v(91.97, 14.25) * mm, "end": v(87.35, 14.25) * mm});
            skLineSegment(sketch, "E23.16.1.1", {"start": v(91.97, 9.63) * mm, "end": v(91.97, 14.25) * mm});
            skLineSegment(sketch, "E23.16.1.2", {"start": v(91.97, 9.63) * mm, "end": v(87.35, 9.63) * mm});
            skLineSegment(sketch, "E23.16.1.3", {"start": v(87.35, 9.63) * mm, "end": v(87.35, 14.25) * mm});
            skLineSegment(sketch, "E23.16.2.0", {"start": v(91.97, 1.55) * mm, "end": v(87.35, 1.55) * mm});
            skLineSegment(sketch, "E23.16.2.1", {"start": v(91.97, -3.07) * mm, "end": v(91.97, 1.55) * mm});
            skLineSegment(sketch, "E23.16.2.2", {"start": v(91.97, -3.07) * mm, "end": v(87.35, -3.07) * mm});
            skLineSegment(sketch, "E23.16.2.3", {"start": v(87.35, -3.07) * mm, "end": v(87.35, 1.55) * mm});
            skLineSegment(sketch, "E23.16.3.0", {"start": v(91.97, -11.15) * mm, "end": v(87.35, -11.15) * mm});
            skLineSegment(sketch, "E23.16.3.1", {"start": v(91.97, -15.77) * mm, "end": v(91.97, -11.15) * mm});
            skLineSegment(sketch, "E23.16.3.2", {"start": v(91.97, -15.77) * mm, "end": v(87.35, -15.77) * mm});
            skLineSegment(sketch, "E23.16.3.3", {"start": v(87.35, -15.77) * mm, "end": v(87.35, -11.15) * mm});
            skLineSegment(sketch, "E23.16.4.0", {"start": v(91.97, -23.85) * mm, "end": v(87.35, -23.85) * mm});
            skLineSegment(sketch, "E23.16.4.1", {"start": v(91.97, -28.47) * mm, "end": v(91.97, -23.85) * mm});
            skLineSegment(sketch, "E23.16.4.2", {"start": v(91.97, -28.47) * mm, "end": v(87.35, -28.47) * mm});
            skLineSegment(sketch, "E23.16.4.3", {"start": v(87.35, -28.47) * mm, "end": v(87.35, -23.85) * mm});
            skLineSegment(sketch, "E23.17.0.0", {"start": v(104.67, 26.95) * mm, "end": v(100.05, 26.95) * mm});
            skLineSegment(sketch, "E23.17.0.1", {"start": v(104.67, 22.33) * mm, "end": v(104.67, 26.95) * mm});
            skLineSegment(sketch, "E23.17.0.2", {"start": v(104.67, 22.33) * mm, "end": v(100.05, 22.33) * mm});
            skLineSegment(sketch, "E23.17.0.3", {"start": v(100.05, 22.33) * mm, "end": v(100.05, 26.95) * mm});
            skLineSegment(sketch, "E23.17.1.0", {"start": v(104.67, 14.25) * mm, "end": v(100.05, 14.25) * mm});
            skLineSegment(sketch, "E23.17.1.1", {"start": v(104.67, 9.63) * mm, "end": v(104.67, 14.25) * mm});
            skLineSegment(sketch, "E23.17.1.2", {"start": v(104.67, 9.63) * mm, "end": v(100.05, 9.63) * mm});
            skLineSegment(sketch, "E23.17.1.3", {"start": v(100.05, 9.63) * mm, "end": v(100.05, 14.25) * mm});
            skLineSegment(sketch, "E23.17.2.0", {"start": v(104.67, 1.55) * mm, "end": v(100.05, 1.55) * mm});
            skLineSegment(sketch, "E23.17.2.1", {"start": v(104.67, -3.07) * mm, "end": v(104.67, 1.55) * mm});
            skLineSegment(sketch, "E23.17.2.2", {"start": v(104.67, -3.07) * mm, "end": v(100.05, -3.07) * mm});
            skLineSegment(sketch, "E23.17.2.3", {"start": v(100.05, -3.07) * mm, "end": v(100.05, 1.55) * mm});
            skLineSegment(sketch, "E23.17.3.0", {"start": v(104.67, -11.15) * mm, "end": v(100.05, -11.15) * mm});
            skLineSegment(sketch, "E23.17.3.1", {"start": v(104.67, -15.77) * mm, "end": v(104.67, -11.15) * mm});
            skLineSegment(sketch, "E23.17.3.2", {"start": v(104.67, -15.77) * mm, "end": v(100.05, -15.77) * mm});
            skLineSegment(sketch, "E23.17.3.3", {"start": v(100.05, -15.77) * mm, "end": v(100.05, -11.15) * mm});
            skLineSegment(sketch, "E23.17.4.0", {"start": v(104.67, -23.85) * mm, "end": v(100.05, -23.85) * mm});
            skLineSegment(sketch, "E23.17.4.1", {"start": v(104.67, -28.47) * mm, "end": v(104.67, -23.85) * mm});
            skLineSegment(sketch, "E23.17.4.2", {"start": v(104.67, -28.47) * mm, "end": v(100.05, -28.47) * mm});
            skLineSegment(sketch, "E23.17.4.3", {"start": v(100.05, -28.47) * mm, "end": v(100.05, -23.85) * mm});
            skLineSegment(sketch, "E23.18.0.0", {"start": v(117.37, 26.95) * mm, "end": v(112.75, 26.95) * mm});
            skLineSegment(sketch, "E23.18.0.1", {"start": v(117.37, 22.33) * mm, "end": v(117.37, 26.95) * mm});
            skLineSegment(sketch, "E23.18.0.2", {"start": v(117.37, 22.33) * mm, "end": v(112.75, 22.33) * mm});
            skLineSegment(sketch, "E23.18.0.3", {"start": v(112.75, 22.33) * mm, "end": v(112.75, 26.95) * mm});
            skLineSegment(sketch, "E23.18.1.0", {"start": v(117.37, 14.25) * mm, "end": v(112.75, 14.25) * mm});
            skLineSegment(sketch, "E23.18.1.1", {"start": v(117.37, 9.63) * mm, "end": v(117.37, 14.25) * mm});
            skLineSegment(sketch, "E23.18.1.2", {"start": v(117.37, 9.63) * mm, "end": v(112.75, 9.63) * mm});
            skLineSegment(sketch, "E23.18.1.3", {"start": v(112.75, 9.63) * mm, "end": v(112.75, 14.25) * mm});
            skLineSegment(sketch, "E23.18.2.0", {"start": v(117.37, 1.55) * mm, "end": v(112.75, 1.55) * mm});
            skLineSegment(sketch, "E23.18.2.1", {"start": v(117.37, -3.07) * mm, "end": v(117.37, 1.55) * mm});
            skLineSegment(sketch, "E23.18.2.2", {"start": v(117.37, -3.07) * mm, "end": v(112.75, -3.07) * mm});
            skLineSegment(sketch, "E23.18.2.3", {"start": v(112.75, -3.07) * mm, "end": v(112.75, 1.55) * mm});
            skLineSegment(sketch, "E23.18.3.0", {"start": v(117.37, -11.15) * mm, "end": v(112.75, -11.15) * mm});
            skLineSegment(sketch, "E23.18.3.1", {"start": v(117.37, -15.77) * mm, "end": v(117.37, -11.15) * mm});
            skLineSegment(sketch, "E23.18.3.2", {"start": v(117.37, -15.77) * mm, "end": v(112.75, -15.77) * mm});
            skLineSegment(sketch, "E23.18.3.3", {"start": v(112.75, -15.77) * mm, "end": v(112.75, -11.15) * mm});
            skLineSegment(sketch, "E23.18.4.0", {"start": v(117.37, -23.85) * mm, "end": v(112.75, -23.85) * mm});
            skLineSegment(sketch, "E23.18.4.1", {"start": v(117.37, -28.47) * mm, "end": v(117.37, -23.85) * mm});
            skLineSegment(sketch, "E23.18.4.2", {"start": v(117.37, -28.47) * mm, "end": v(112.75, -28.47) * mm});
            skLineSegment(sketch, "E23.18.4.3", {"start": v(112.75, -28.47) * mm, "end": v(112.75, -23.85) * mm});
            skLineSegment(sketch, "E23.direction1", {"start": v(-115.85, 26.95) * mm, "end": v(-103.15, 26.95) * mm, "construction": true});
            skLineSegment(sketch, "E23.direction2", {"start": v(-115.85, 26.95) * mm, "end": v(-115.85, 14.25) * mm, "construction": true});
            skSolve(sketch);
        }
        {
            var Q0;
            Q0=makeQuery(id+"F0.imprint","IMPRINT",FACE,{"disambiguationData":[TD([[makeQuery(id+"F0.imprint","IMPRINT",EDGE,{"derivedFrom":sQuery(id+"F0.wireOp",EDGE,"E0.rect.bottom")}),-1.0]])]});
            extrude(context, id + "F1", {"entities" : qUnion([Q0]), "depth" : 3.17 * mm});
        }
    });
